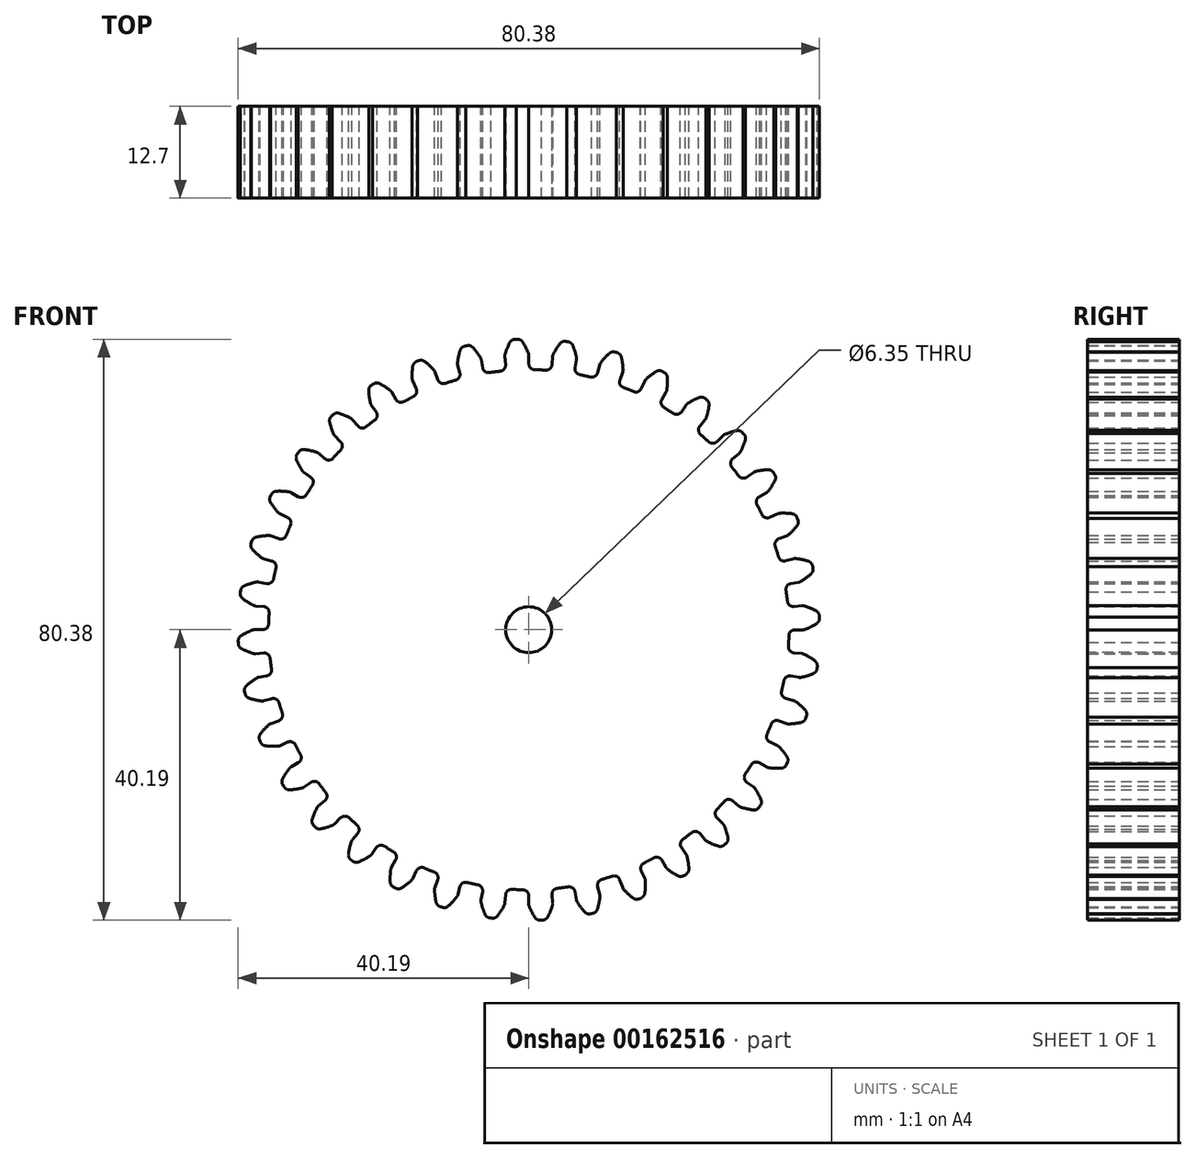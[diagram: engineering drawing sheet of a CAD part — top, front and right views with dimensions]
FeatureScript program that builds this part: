
annotation { "Feature Type Name" : "Feature", "Feature Type Description" : "" }
export const myFeature = defineFeature(function(context is Context, id is Id, definition is map)
    precondition{}
    {
        {
            var Q0;
            Q0=qCreatedBy(makeId("Front.planeOp"),FACE);
            var sketch = newSketch(context, id + "F0", { "sketchPlane" : qUnion([Q0])});
            skArc(sketch, "E0", {"start": v(-3.94, 35.77) * mm, "mid": v(-4.7, 35.68) * mm, "end": v(-5.45, 35.57) * mm});
            skArc(sketch, "E1", {"start": v(-0.05, 38.25) * mm, "mid": v(-0.42, 39.05) * mm, "end": v(-0.85, 39.8) * mm});
            skLineSegment(sketch, "E2", {"start": v(0, 37.94) * mm, "end": v(0, 36.8) * mm});
            skLineSegment(sketch, "E3", {"start": v(-1.58, 40.18) * mm, "end": v(-1.76, 40.18) * mm});
            skLineSegment(sketch, "E4.MirrorCS", {"start": v(-1.93, 40.17) * mm, "end": v(-1.75, 40.18) * mm});
            skArc(sketch, "E5.MirrorCS", {"start": v(-3.28, 38.11) * mm, "mid": v(-2.99, 38.93) * mm, "end": v(-2.62, 39.73) * mm});
            skLineSegment(sketch, "E6.MirrorCS", {"start": v(-3.31, 37.8) * mm, "end": v(-3.21, 36.66) * mm});
            skPoint(sketch, "E7.visualSharp", {"position": v(-3.14, 35.85) * mm});
            skArc(sketch, "E7.filletArc", {"start": v(-3.94, 35.77) * mm, "mid": v(-3.4, 36.07) * mm, "end": v(-3.21, 36.66) * mm});
            skPoint(sketch, "E8.visualSharp", {"position": v(0, 35.98) * mm});
            skArc(sketch, "E8.filletArc", {"start": v(0, 36.8) * mm, "mid": v(0.24, 36.22) * mm, "end": v(0.81, 35.97) * mm});
            skArc(sketch, "E9.filletArc", {"start": v(-1.93, 40.17) * mm, "mid": v(-2.34, 40.04) * mm, "end": v(-2.62, 39.73) * mm});
            skArc(sketch, "E10.filletArc", {"start": v(-0.85, 39.8) * mm, "mid": v(-1.16, 40.1) * mm, "end": v(-1.58, 40.18) * mm});
            skPoint(sketch, "E11.visualSharp", {"position": v(0, 38.1) * mm});
            skArc(sketch, "E11.filletArc", {"start": v(0, 37.94) * mm, "mid": v(0, 38.1) * mm, "end": v(-0.05, 38.25) * mm});
            skPoint(sketch, "E12.visualSharp", {"position": v(-3.33, 37.95) * mm});
            skArc(sketch, "E12.filletArc", {"start": v(-3.28, 38.11) * mm, "mid": v(-3.31, 37.96) * mm, "end": v(-3.31, 37.8) * mm});
            skArc(sketch, "E13.1.0", {"start": v(-10.1, 34.54) * mm, "mid": v(-9.6, 34.93) * mm, "end": v(-9.53, 35.55) * mm});
            skLineSegment(sketch, "E13.1.1", {"start": v(-9.83, 36.65) * mm, "end": v(-9.53, 35.55) * mm});
            skArc(sketch, "E13.1.2", {"start": v(-9.85, 36.96) * mm, "mid": v(-9.85, 36.8) * mm, "end": v(-9.83, 36.65) * mm});
            skArc(sketch, "E13.1.3", {"start": v(-9.85, 36.96) * mm, "mid": v(-9.7, 37.82) * mm, "end": v(-9.48, 38.67) * mm});
            skArc(sketch, "E13.1.4", {"start": v(-8.88, 39.22) * mm, "mid": v(-9.25, 39.03) * mm, "end": v(-9.48, 38.67) * mm});
            skLineSegment(sketch, "E13.1.5", {"start": v(-8.88, 39.22) * mm, "end": v(-8.7, 39.26) * mm});
            skLineSegment(sketch, "E13.1.6", {"start": v(-8.53, 39.3) * mm, "end": v(-8.7, 39.26) * mm});
            skArc(sketch, "E13.1.7", {"start": v(-7.75, 39.05) * mm, "mid": v(-8.1, 39.28) * mm, "end": v(-8.53, 39.3) * mm});
            skArc(sketch, "E13.1.8", {"start": v(-6.7, 37.66) * mm, "mid": v(-7.2, 38.38) * mm, "end": v(-7.75, 39.05) * mm});
            skArc(sketch, "E13.1.9", {"start": v(-6.58, 37.37) * mm, "mid": v(-6.62, 37.52) * mm, "end": v(-6.7, 37.66) * mm});
            skLineSegment(sketch, "E13.1.10", {"start": v(-6.58, 37.37) * mm, "end": v(-6.39, 36.24) * mm});
            skArc(sketch, "E13.1.11", {"start": v(-6.39, 36.24) * mm, "mid": v(-6.06, 35.71) * mm, "end": v(-5.45, 35.57) * mm});
            skArc(sketch, "E13.2.0", {"start": v(-15.94, 32.26) * mm, "mid": v(-15.52, 32.73) * mm, "end": v(-15.56, 33.35) * mm});
            skLineSegment(sketch, "E13.2.1", {"start": v(-16.04, 34.38) * mm, "end": v(-15.56, 33.35) * mm});
            skArc(sketch, "E13.2.2", {"start": v(-16.12, 34.7) * mm, "mid": v(-16.1, 34.53) * mm, "end": v(-16.04, 34.38) * mm});
            skArc(sketch, "E13.2.3", {"start": v(-16.12, 34.7) * mm, "mid": v(-16.13, 35.56) * mm, "end": v(-16.05, 36.43) * mm});
            skArc(sketch, "E13.2.4", {"start": v(-15.55, 37.09) * mm, "mid": v(-15.89, 36.83) * mm, "end": v(-16.05, 36.43) * mm});
            skLineSegment(sketch, "E13.2.5", {"start": v(-15.55, 37.09) * mm, "end": v(-15.39, 37.16) * mm});
            skLineSegment(sketch, "E13.2.6", {"start": v(-15.23, 37.22) * mm, "end": v(-15.4, 37.16) * mm});
            skArc(sketch, "E13.2.7", {"start": v(-14.41, 37.11) * mm, "mid": v(-14.8, 37.28) * mm, "end": v(-15.23, 37.22) * mm});
            skArc(sketch, "E13.2.8", {"start": v(-13.13, 35.93) * mm, "mid": v(-13.75, 36.55) * mm, "end": v(-14.41, 37.11) * mm});
            skArc(sketch, "E13.2.9", {"start": v(-12.97, 35.66) * mm, "mid": v(-13.04, 35.8) * mm, "end": v(-13.13, 35.93) * mm});
            skLineSegment(sketch, "E13.2.10", {"start": v(-12.97, 35.66) * mm, "end": v(-12.58, 34.58) * mm});
            skArc(sketch, "E13.2.11", {"start": v(-12.58, 34.58) * mm, "mid": v(-12.17, 34.12) * mm, "end": v(-11.54, 34.08) * mm});
            skArc(sketch, "E13.3.0", {"start": v(-21.3, 29) * mm, "mid": v(-20.97, 29.54) * mm, "end": v(-21.11, 30.15) * mm});
            skLineSegment(sketch, "E13.3.1", {"start": v(-21.77, 31.08) * mm, "end": v(-21.11, 30.15) * mm});
            skArc(sketch, "E13.3.2", {"start": v(-21.9, 31.37) * mm, "mid": v(-21.85, 31.21) * mm, "end": v(-21.77, 31.08) * mm});
            skArc(sketch, "E13.3.3", {"start": v(-21.9, 31.37) * mm, "mid": v(-22.06, 32.22) * mm, "end": v(-22.13, 33.1) * mm});
            skArc(sketch, "E13.3.4", {"start": v(-21.76, 33.82) * mm, "mid": v(-22.04, 33.5) * mm, "end": v(-22.13, 33.1) * mm});
            skLineSegment(sketch, "E13.3.5", {"start": v(-21.76, 33.82) * mm, "end": v(-21.6, 33.92) * mm});
            skLineSegment(sketch, "E13.3.6", {"start": v(-21.46, 34.01) * mm, "end": v(-21.6, 33.92) * mm});
            skArc(sketch, "E13.3.7", {"start": v(-20.64, 34.05) * mm, "mid": v(-21.05, 34.14) * mm, "end": v(-21.46, 34.01) * mm});
            skArc(sketch, "E13.3.8", {"start": v(-19.17, 33.1) * mm, "mid": v(-19.88, 33.6) * mm, "end": v(-20.64, 34.05) * mm});
            skArc(sketch, "E13.3.9", {"start": v(-18.96, 32.86) * mm, "mid": v(-19.06, 33) * mm, "end": v(-19.17, 33.1) * mm});
            skLineSegment(sketch, "E13.3.10", {"start": v(-18.96, 32.86) * mm, "end": v(-18.4, 31.87) * mm});
            skArc(sketch, "E13.3.11", {"start": v(-18.4, 31.87) * mm, "mid": v(-17.9, 31.49) * mm, "end": v(-17.29, 31.56) * mm});
            skArc(sketch, "E13.4.0", {"start": v(-26.01, 24.86) * mm, "mid": v(-25.78, 25.45) * mm, "end": v(-26.03, 26.02) * mm});
            skLineSegment(sketch, "E13.4.1", {"start": v(-26.83, 26.82) * mm, "end": v(-26.03, 26.02) * mm});
            skArc(sketch, "E13.4.2", {"start": v(-27.01, 27.09) * mm, "mid": v(-26.94, 26.95) * mm, "end": v(-26.83, 26.82) * mm});
            skArc(sketch, "E13.4.3", {"start": v(-27.01, 27.09) * mm, "mid": v(-27.32, 27.9) * mm, "end": v(-27.54, 28.75) * mm});
            skArc(sketch, "E13.4.4", {"start": v(-27.3, 29.53) * mm, "mid": v(-27.53, 29.17) * mm, "end": v(-27.54, 28.75) * mm});
            skLineSegment(sketch, "E13.4.5", {"start": v(-27.3, 29.53) * mm, "end": v(-27.17, 29.65) * mm});
            skLineSegment(sketch, "E13.4.6", {"start": v(-27.04, 29.77) * mm, "end": v(-27.17, 29.65) * mm});
            skArc(sketch, "E13.4.7", {"start": v(-26.24, 29.94) * mm, "mid": v(-26.66, 29.96) * mm, "end": v(-27.04, 29.77) * mm});
            skArc(sketch, "E13.4.8", {"start": v(-24.63, 29.27) * mm, "mid": v(-25.42, 29.64) * mm, "end": v(-26.24, 29.94) * mm});
            skArc(sketch, "E13.4.9", {"start": v(-24.38, 29.07) * mm, "mid": v(-24.5, 29.18) * mm, "end": v(-24.63, 29.27) * mm});
            skLineSegment(sketch, "E13.4.10", {"start": v(-24.38, 29.07) * mm, "end": v(-23.65, 28.2) * mm});
            skArc(sketch, "E13.4.11", {"start": v(-23.65, 28.2) * mm, "mid": v(-23.1, 27.9) * mm, "end": v(-22.5, 28.08) * mm});
            skArc(sketch, "E13.5.0", {"start": v(-29.93, 19.97) * mm, "mid": v(-29.8, 20.58) * mm, "end": v(-30.15, 21.1) * mm});
            skLineSegment(sketch, "E13.5.1", {"start": v(-31.08, 21.76) * mm, "end": v(-30.15, 21.1) * mm});
            skArc(sketch, "E13.5.2", {"start": v(-31.3, 21.98) * mm, "mid": v(-31.2, 21.86) * mm, "end": v(-31.08, 21.76) * mm});
            skArc(sketch, "E13.5.3", {"start": v(-31.3, 21.98) * mm, "mid": v(-31.75, 22.74) * mm, "end": v(-32.12, 23.53) * mm});
            skArc(sketch, "E13.5.4", {"start": v(-32.01, 24.34) * mm, "mid": v(-32.17, 23.95) * mm, "end": v(-32.12, 23.53) * mm});
            skLineSegment(sketch, "E13.5.5", {"start": v(-32.01, 24.34) * mm, "end": v(-31.9, 24.48) * mm});
            skLineSegment(sketch, "E13.5.6", {"start": v(-31.8, 24.62) * mm, "end": v(-31.9, 24.48) * mm});
            skArc(sketch, "E13.5.7", {"start": v(-31.04, 24.93) * mm, "mid": v(-31.46, 24.88) * mm, "end": v(-31.8, 24.62) * mm});
            skArc(sketch, "E13.5.8", {"start": v(-29.34, 24.55) * mm, "mid": v(-30.18, 24.78) * mm, "end": v(-31.04, 24.93) * mm});
            skArc(sketch, "E13.5.9", {"start": v(-29.06, 24.4) * mm, "mid": v(-29.2, 24.49) * mm, "end": v(-29.34, 24.55) * mm});
            skLineSegment(sketch, "E13.5.10", {"start": v(-29.06, 24.4) * mm, "end": v(-28.2, 23.66) * mm});
            skArc(sketch, "E13.5.11", {"start": v(-28.2, 23.66) * mm, "mid": v(-27.6, 23.47) * mm, "end": v(-27.04, 23.74) * mm});
            skArc(sketch, "E13.6.0", {"start": v(-32.95, 14.47) * mm, "mid": v(-32.93, 15.1) * mm, "end": v(-33.36, 15.55) * mm});
            skLineSegment(sketch, "E13.6.1", {"start": v(-34.4, 16.03) * mm, "end": v(-33.36, 15.55) * mm});
            skArc(sketch, "E13.6.2", {"start": v(-34.65, 16.21) * mm, "mid": v(-34.53, 16.1) * mm, "end": v(-34.4, 16.03) * mm});
            skArc(sketch, "E13.6.3", {"start": v(-34.65, 16.21) * mm, "mid": v(-35.21, 16.88) * mm, "end": v(-35.71, 17.6) * mm});
            skArc(sketch, "E13.6.4", {"start": v(-35.75, 18.41) * mm, "mid": v(-35.84, 18) * mm, "end": v(-35.71, 17.6) * mm});
            skLineSegment(sketch, "E13.6.5", {"start": v(-35.75, 18.41) * mm, "end": v(-35.67, 18.57) * mm});
            skLineSegment(sketch, "E13.6.6", {"start": v(-35.59, 18.73) * mm, "end": v(-35.67, 18.57) * mm});
            skArc(sketch, "E13.6.7", {"start": v(-34.9, 19.16) * mm, "mid": v(-35.3, 19.04) * mm, "end": v(-35.59, 18.73) * mm});
            skArc(sketch, "E13.6.8", {"start": v(-33.16, 19.08) * mm, "mid": v(-34.02, 19.16) * mm, "end": v(-34.9, 19.16) * mm});
            skArc(sketch, "E13.6.9", {"start": v(-32.85, 18.98) * mm, "mid": v(-33, 19.04) * mm, "end": v(-33.16, 19.08) * mm});
            skLineSegment(sketch, "E13.6.10", {"start": v(-32.85, 18.98) * mm, "end": v(-31.87, 18.4) * mm});
            skArc(sketch, "E13.6.11", {"start": v(-31.87, 18.4) * mm, "mid": v(-31.25, 18.32) * mm, "end": v(-30.75, 18.69) * mm});
            skArc(sketch, "E13.7.0", {"start": v(-34.96, 8.53) * mm, "mid": v(-35.05, 9.15) * mm, "end": v(-35.55, 9.52) * mm});
            skLineSegment(sketch, "E13.7.1", {"start": v(-36.65, 9.81) * mm, "end": v(-35.55, 9.52) * mm});
            skArc(sketch, "E13.7.2", {"start": v(-36.94, 9.95) * mm, "mid": v(-36.8, 9.87) * mm, "end": v(-36.65, 9.81) * mm});
            skArc(sketch, "E13.7.3", {"start": v(-36.94, 9.95) * mm, "mid": v(-37.6, 10.5) * mm, "end": v(-38.23, 11.12) * mm});
            skArc(sketch, "E13.7.4", {"start": v(-38.4, 11.92) * mm, "mid": v(-38.42, 11.5) * mm, "end": v(-38.23, 11.12) * mm});
            skLineSegment(sketch, "E13.7.5", {"start": v(-38.4, 11.92) * mm, "end": v(-38.36, 12.1) * mm});
            skLineSegment(sketch, "E13.7.6", {"start": v(-38.3, 12.26) * mm, "end": v(-38.36, 12.1) * mm});
            skArc(sketch, "E13.7.7", {"start": v(-37.7, 12.81) * mm, "mid": v(-38.07, 12.62) * mm, "end": v(-38.3, 12.26) * mm});
            skArc(sketch, "E13.7.8", {"start": v(-35.97, 13.03) * mm, "mid": v(-36.83, 12.96) * mm, "end": v(-37.7, 12.81) * mm});
            skArc(sketch, "E13.7.9", {"start": v(-35.65, 12.98) * mm, "mid": v(-35.8, 13.02) * mm, "end": v(-35.97, 13.03) * mm});
            skLineSegment(sketch, "E13.7.10", {"start": v(-35.65, 12.98) * mm, "end": v(-34.58, 12.6) * mm});
            skArc(sketch, "E13.7.11", {"start": v(-34.58, 12.6) * mm, "mid": v(-33.96, 12.61) * mm, "end": v(-33.53, 13.07) * mm});
            skArc(sketch, "E13.8.0", {"start": v(-35.9, 2.33) * mm, "mid": v(-36.1, 2.92) * mm, "end": v(-36.66, 3.2) * mm});
            skLineSegment(sketch, "E13.8.1", {"start": v(-37.8, 3.3) * mm, "end": v(-36.66, 3.2) * mm});
            skArc(sketch, "E13.8.2", {"start": v(-38.1, 3.39) * mm, "mid": v(-37.96, 3.33) * mm, "end": v(-37.8, 3.3) * mm});
            skArc(sketch, "E13.8.3", {"start": v(-38.1, 3.39) * mm, "mid": v(-38.86, 3.82) * mm, "end": v(-39.58, 4.32) * mm});
            skArc(sketch, "E13.8.4", {"start": v(-39.9, 5.07) * mm, "mid": v(-39.84, 4.65) * mm, "end": v(-39.58, 4.32) * mm});
            skLineSegment(sketch, "E13.8.5", {"start": v(-39.9, 5.07) * mm, "end": v(-39.87, 5.25) * mm});
            skLineSegment(sketch, "E13.8.6", {"start": v(-39.85, 5.43) * mm, "end": v(-39.87, 5.25) * mm});
            skArc(sketch, "E13.8.7", {"start": v(-39.35, 6.07) * mm, "mid": v(-39.68, 5.82) * mm, "end": v(-39.85, 5.43) * mm});
            skArc(sketch, "E13.8.8", {"start": v(-37.68, 6.6) * mm, "mid": v(-38.53, 6.37) * mm, "end": v(-39.35, 6.07) * mm});
            skArc(sketch, "E13.8.9", {"start": v(-37.36, 6.6) * mm, "mid": v(-37.52, 6.6) * mm, "end": v(-37.68, 6.6) * mm});
            skLineSegment(sketch, "E13.8.10", {"start": v(-37.36, 6.6) * mm, "end": v(-36.24, 6.4) * mm});
            skArc(sketch, "E13.8.11", {"start": v(-36.24, 6.4) * mm, "mid": v(-35.63, 6.52) * mm, "end": v(-35.29, 7.04) * mm});
            skArc(sketch, "E13.9.0", {"start": v(-35.77, -3.94) * mm, "mid": v(-36.07, -3.4) * mm, "end": v(-36.66, -3.21) * mm});
            skLineSegment(sketch, "E13.9.1", {"start": v(-37.8, -3.31) * mm, "end": v(-36.66, -3.21) * mm});
            skArc(sketch, "E13.9.2", {"start": v(-38.11, -3.28) * mm, "mid": v(-37.96, -3.31) * mm, "end": v(-37.8, -3.31) * mm});
            skArc(sketch, "E13.9.3", {"start": v(-38.11, -3.28) * mm, "mid": v(-38.93, -2.99) * mm, "end": v(-39.73, -2.62) * mm});
            skArc(sketch, "E13.9.4", {"start": v(-40.17, -1.93) * mm, "mid": v(-40.04, -2.34) * mm, "end": v(-39.73, -2.62) * mm});
            skLineSegment(sketch, "E13.9.5", {"start": v(-40.17, -1.93) * mm, "end": v(-40.18, -1.75) * mm});
            skLineSegment(sketch, "E13.9.6", {"start": v(-40.18, -1.58) * mm, "end": v(-40.18, -1.76) * mm});
            skArc(sketch, "E13.9.7", {"start": v(-39.8, -0.85) * mm, "mid": v(-40.1, -1.16) * mm, "end": v(-40.18, -1.58) * mm});
            skArc(sketch, "E13.9.8", {"start": v(-38.25, -0.05) * mm, "mid": v(-39.05, -0.42) * mm, "end": v(-39.8, -0.85) * mm});
            skArc(sketch, "E13.9.9", {"start": v(-37.94, 0) * mm, "mid": v(-38.1, 0) * mm, "end": v(-38.25, -0.05) * mm});
            skLineSegment(sketch, "E13.9.10", {"start": v(-37.94, 0) * mm, "end": v(-36.8, 0) * mm});
            skArc(sketch, "E13.9.11", {"start": v(-36.8, 0) * mm, "mid": v(-36.22, 0.24) * mm, "end": v(-35.97, 0.81) * mm});
            skArc(sketch, "E13.10.0", {"start": v(-34.54, -10.1) * mm, "mid": v(-34.93, -9.6) * mm, "end": v(-35.55, -9.53) * mm});
            skLineSegment(sketch, "E13.10.1", {"start": v(-36.65, -9.83) * mm, "end": v(-35.55, -9.53) * mm});
            skArc(sketch, "E13.10.2", {"start": v(-36.96, -9.85) * mm, "mid": v(-36.8, -9.85) * mm, "end": v(-36.65, -9.83) * mm});
            skArc(sketch, "E13.10.3", {"start": v(-36.96, -9.85) * mm, "mid": v(-37.82, -9.7) * mm, "end": v(-38.67, -9.48) * mm});
            skArc(sketch, "E13.10.4", {"start": v(-39.22, -8.88) * mm, "mid": v(-39.03, -9.25) * mm, "end": v(-38.67, -9.48) * mm});
            skLineSegment(sketch, "E13.10.5", {"start": v(-39.22, -8.88) * mm, "end": v(-39.26, -8.7) * mm});
            skLineSegment(sketch, "E13.10.6", {"start": v(-39.3, -8.53) * mm, "end": v(-39.26, -8.7) * mm});
            skArc(sketch, "E13.10.7", {"start": v(-39.05, -7.75) * mm, "mid": v(-39.28, -8.1) * mm, "end": v(-39.3, -8.53) * mm});
            skArc(sketch, "E13.10.8", {"start": v(-37.66, -6.7) * mm, "mid": v(-38.38, -7.2) * mm, "end": v(-39.05, -7.75) * mm});
            skArc(sketch, "E13.10.9", {"start": v(-37.37, -6.58) * mm, "mid": v(-37.52, -6.62) * mm, "end": v(-37.66, -6.7) * mm});
            skLineSegment(sketch, "E13.10.10", {"start": v(-37.37, -6.58) * mm, "end": v(-36.24, -6.39) * mm});
            skArc(sketch, "E13.10.11", {"start": v(-36.24, -6.39) * mm, "mid": v(-35.71, -6.06) * mm, "end": v(-35.57, -5.45) * mm});
            skArc(sketch, "E13.11.0", {"start": v(-32.26, -15.94) * mm, "mid": v(-32.73, -15.52) * mm, "end": v(-33.35, -15.56) * mm});
            skLineSegment(sketch, "E13.11.1", {"start": v(-34.38, -16.04) * mm, "end": v(-33.35, -15.56) * mm});
            skArc(sketch, "E13.11.2", {"start": v(-34.7, -16.12) * mm, "mid": v(-34.53, -16.1) * mm, "end": v(-34.38, -16.04) * mm});
            skArc(sketch, "E13.11.3", {"start": v(-34.7, -16.12) * mm, "mid": v(-35.56, -16.13) * mm, "end": v(-36.43, -16.05) * mm});
            skArc(sketch, "E13.11.4", {"start": v(-37.09, -15.55) * mm, "mid": v(-36.83, -15.89) * mm, "end": v(-36.43, -16.05) * mm});
            skLineSegment(sketch, "E13.11.5", {"start": v(-37.09, -15.55) * mm, "end": v(-37.16, -15.39) * mm});
            skLineSegment(sketch, "E13.11.6", {"start": v(-37.22, -15.23) * mm, "end": v(-37.16, -15.4) * mm});
            skArc(sketch, "E13.11.7", {"start": v(-37.11, -14.41) * mm, "mid": v(-37.28, -14.8) * mm, "end": v(-37.22, -15.23) * mm});
            skArc(sketch, "E13.11.8", {"start": v(-35.93, -13.13) * mm, "mid": v(-36.55, -13.75) * mm, "end": v(-37.11, -14.41) * mm});
            skArc(sketch, "E13.11.9", {"start": v(-35.66, -12.97) * mm, "mid": v(-35.8, -13.04) * mm, "end": v(-35.93, -13.13) * mm});
            skLineSegment(sketch, "E13.11.10", {"start": v(-35.66, -12.97) * mm, "end": v(-34.58, -12.58) * mm});
            skArc(sketch, "E13.11.11", {"start": v(-34.58, -12.58) * mm, "mid": v(-34.12, -12.17) * mm, "end": v(-34.08, -11.54) * mm});
            skArc(sketch, "E13.12.0", {"start": v(-29, -21.3) * mm, "mid": v(-29.54, -20.97) * mm, "end": v(-30.15, -21.11) * mm});
            skLineSegment(sketch, "E13.12.1", {"start": v(-31.08, -21.77) * mm, "end": v(-30.15, -21.11) * mm});
            skArc(sketch, "E13.12.2", {"start": v(-31.37, -21.9) * mm, "mid": v(-31.21, -21.85) * mm, "end": v(-31.08, -21.77) * mm});
            skArc(sketch, "E13.12.3", {"start": v(-31.37, -21.9) * mm, "mid": v(-32.22, -22.06) * mm, "end": v(-33.1, -22.13) * mm});
            skArc(sketch, "E13.12.4", {"start": v(-33.82, -21.76) * mm, "mid": v(-33.5, -22.04) * mm, "end": v(-33.1, -22.13) * mm});
            skLineSegment(sketch, "E13.12.5", {"start": v(-33.82, -21.76) * mm, "end": v(-33.92, -21.6) * mm});
            skLineSegment(sketch, "E13.12.6", {"start": v(-34.01, -21.46) * mm, "end": v(-33.92, -21.6) * mm});
            skArc(sketch, "E13.12.7", {"start": v(-34.05, -20.64) * mm, "mid": v(-34.14, -21.05) * mm, "end": v(-34.01, -21.46) * mm});
            skArc(sketch, "E13.12.8", {"start": v(-33.1, -19.17) * mm, "mid": v(-33.6, -19.88) * mm, "end": v(-34.05, -20.64) * mm});
            skArc(sketch, "E13.12.9", {"start": v(-32.86, -18.96) * mm, "mid": v(-33, -19.06) * mm, "end": v(-33.1, -19.17) * mm});
            skLineSegment(sketch, "E13.12.10", {"start": v(-32.86, -18.96) * mm, "end": v(-31.87, -18.4) * mm});
            skArc(sketch, "E13.12.11", {"start": v(-31.87, -18.4) * mm, "mid": v(-31.49, -17.9) * mm, "end": v(-31.56, -17.29) * mm});
            skArc(sketch, "E13.13.0", {"start": v(-24.86, -26.01) * mm, "mid": v(-25.45, -25.78) * mm, "end": v(-26.02, -26.03) * mm});
            skLineSegment(sketch, "E13.13.1", {"start": v(-26.82, -26.83) * mm, "end": v(-26.02, -26.03) * mm});
            skArc(sketch, "E13.13.2", {"start": v(-27.09, -27.01) * mm, "mid": v(-26.95, -26.94) * mm, "end": v(-26.82, -26.83) * mm});
            skArc(sketch, "E13.13.3", {"start": v(-27.09, -27.01) * mm, "mid": v(-27.9, -27.32) * mm, "end": v(-28.75, -27.54) * mm});
            skArc(sketch, "E13.13.4", {"start": v(-29.53, -27.3) * mm, "mid": v(-29.17, -27.53) * mm, "end": v(-28.75, -27.54) * mm});
            skLineSegment(sketch, "E13.13.5", {"start": v(-29.53, -27.3) * mm, "end": v(-29.65, -27.17) * mm});
            skLineSegment(sketch, "E13.13.6", {"start": v(-29.77, -27.04) * mm, "end": v(-29.65, -27.17) * mm});
            skArc(sketch, "E13.13.7", {"start": v(-29.94, -26.24) * mm, "mid": v(-29.96, -26.66) * mm, "end": v(-29.77, -27.04) * mm});
            skArc(sketch, "E13.13.8", {"start": v(-29.27, -24.63) * mm, "mid": v(-29.64, -25.42) * mm, "end": v(-29.94, -26.24) * mm});
            skArc(sketch, "E13.13.9", {"start": v(-29.07, -24.38) * mm, "mid": v(-29.18, -24.5) * mm, "end": v(-29.27, -24.63) * mm});
            skLineSegment(sketch, "E13.13.10", {"start": v(-29.07, -24.38) * mm, "end": v(-28.2, -23.65) * mm});
            skArc(sketch, "E13.13.11", {"start": v(-28.2, -23.65) * mm, "mid": v(-27.9, -23.1) * mm, "end": v(-28.08, -22.5) * mm});
            skArc(sketch, "E13.14.0", {"start": v(-19.97, -29.93) * mm, "mid": v(-20.58, -29.8) * mm, "end": v(-21.1, -30.15) * mm});
            skLineSegment(sketch, "E13.14.1", {"start": v(-21.76, -31.08) * mm, "end": v(-21.1, -30.15) * mm});
            skArc(sketch, "E13.14.2", {"start": v(-21.98, -31.3) * mm, "mid": v(-21.86, -31.2) * mm, "end": v(-21.76, -31.08) * mm});
            skArc(sketch, "E13.14.3", {"start": v(-21.98, -31.3) * mm, "mid": v(-22.74, -31.75) * mm, "end": v(-23.53, -32.12) * mm});
            skArc(sketch, "E13.14.4", {"start": v(-24.34, -32.01) * mm, "mid": v(-23.95, -32.17) * mm, "end": v(-23.53, -32.12) * mm});
            skLineSegment(sketch, "E13.14.5", {"start": v(-24.34, -32.01) * mm, "end": v(-24.48, -31.9) * mm});
            skLineSegment(sketch, "E13.14.6", {"start": v(-24.62, -31.8) * mm, "end": v(-24.48, -31.9) * mm});
            skArc(sketch, "E13.14.7", {"start": v(-24.93, -31.04) * mm, "mid": v(-24.88, -31.46) * mm, "end": v(-24.62, -31.8) * mm});
            skArc(sketch, "E13.14.8", {"start": v(-24.55, -29.34) * mm, "mid": v(-24.78, -30.18) * mm, "end": v(-24.93, -31.04) * mm});
            skArc(sketch, "E13.14.9", {"start": v(-24.4, -29.06) * mm, "mid": v(-24.49, -29.2) * mm, "end": v(-24.55, -29.34) * mm});
            skLineSegment(sketch, "E13.14.10", {"start": v(-24.4, -29.06) * mm, "end": v(-23.66, -28.2) * mm});
            skArc(sketch, "E13.14.11", {"start": v(-23.66, -28.2) * mm, "mid": v(-23.47, -27.6) * mm, "end": v(-23.74, -27.04) * mm});
            skArc(sketch, "E13.15.0", {"start": v(-14.47, -32.95) * mm, "mid": v(-15.1, -32.93) * mm, "end": v(-15.55, -33.36) * mm});
            skLineSegment(sketch, "E13.15.1", {"start": v(-16.03, -34.4) * mm, "end": v(-15.55, -33.36) * mm});
            skArc(sketch, "E13.15.2", {"start": v(-16.21, -34.65) * mm, "mid": v(-16.1, -34.53) * mm, "end": v(-16.03, -34.4) * mm});
            skArc(sketch, "E13.15.3", {"start": v(-16.21, -34.65) * mm, "mid": v(-16.88, -35.21) * mm, "end": v(-17.6, -35.71) * mm});
            skArc(sketch, "E13.15.4", {"start": v(-18.41, -35.75) * mm, "mid": v(-18, -35.84) * mm, "end": v(-17.6, -35.71) * mm});
            skLineSegment(sketch, "E13.15.5", {"start": v(-18.41, -35.75) * mm, "end": v(-18.57, -35.67) * mm});
            skLineSegment(sketch, "E13.15.6", {"start": v(-18.73, -35.59) * mm, "end": v(-18.57, -35.67) * mm});
            skArc(sketch, "E13.15.7", {"start": v(-19.16, -34.9) * mm, "mid": v(-19.04, -35.3) * mm, "end": v(-18.73, -35.59) * mm});
            skArc(sketch, "E13.15.8", {"start": v(-19.08, -33.16) * mm, "mid": v(-19.16, -34.02) * mm, "end": v(-19.16, -34.9) * mm});
            skArc(sketch, "E13.15.9", {"start": v(-18.98, -32.85) * mm, "mid": v(-19.04, -33) * mm, "end": v(-19.08, -33.16) * mm});
            skLineSegment(sketch, "E13.15.10", {"start": v(-18.98, -32.85) * mm, "end": v(-18.4, -31.87) * mm});
            skArc(sketch, "E13.15.11", {"start": v(-18.4, -31.87) * mm, "mid": v(-18.32, -31.25) * mm, "end": v(-18.69, -30.75) * mm});
            skArc(sketch, "E13.16.0", {"start": v(-8.53, -34.96) * mm, "mid": v(-9.15, -35.05) * mm, "end": v(-9.52, -35.55) * mm});
            skLineSegment(sketch, "E13.16.1", {"start": v(-9.81, -36.65) * mm, "end": v(-9.52, -35.55) * mm});
            skArc(sketch, "E13.16.2", {"start": v(-9.95, -36.94) * mm, "mid": v(-9.87, -36.8) * mm, "end": v(-9.81, -36.65) * mm});
            skArc(sketch, "E13.16.3", {"start": v(-9.95, -36.94) * mm, "mid": v(-10.5, -37.6) * mm, "end": v(-11.12, -38.23) * mm});
            skArc(sketch, "E13.16.4", {"start": v(-11.92, -38.4) * mm, "mid": v(-11.5, -38.42) * mm, "end": v(-11.12, -38.23) * mm});
            skLineSegment(sketch, "E13.16.5", {"start": v(-11.92, -38.4) * mm, "end": v(-12.1, -38.36) * mm});
            skLineSegment(sketch, "E13.16.6", {"start": v(-12.26, -38.3) * mm, "end": v(-12.1, -38.36) * mm});
            skArc(sketch, "E13.16.7", {"start": v(-12.81, -37.7) * mm, "mid": v(-12.62, -38.07) * mm, "end": v(-12.26, -38.3) * mm});
            skArc(sketch, "E13.16.8", {"start": v(-13.03, -35.97) * mm, "mid": v(-12.96, -36.83) * mm, "end": v(-12.81, -37.7) * mm});
            skArc(sketch, "E13.16.9", {"start": v(-12.98, -35.65) * mm, "mid": v(-13.02, -35.8) * mm, "end": v(-13.03, -35.97) * mm});
            skLineSegment(sketch, "E13.16.10", {"start": v(-12.98, -35.65) * mm, "end": v(-12.6, -34.58) * mm});
            skArc(sketch, "E13.16.11", {"start": v(-12.6, -34.58) * mm, "mid": v(-12.61, -33.96) * mm, "end": v(-13.07, -33.53) * mm});
            skArc(sketch, "E13.17.0", {"start": v(-2.33, -35.9) * mm, "mid": v(-2.92, -36.1) * mm, "end": v(-3.2, -36.66) * mm});
            skLineSegment(sketch, "E13.17.1", {"start": v(-3.3, -37.8) * mm, "end": v(-3.2, -36.66) * mm});
            skArc(sketch, "E13.17.2", {"start": v(-3.39, -38.1) * mm, "mid": v(-3.33, -37.96) * mm, "end": v(-3.3, -37.8) * mm});
            skArc(sketch, "E13.17.3", {"start": v(-3.39, -38.1) * mm, "mid": v(-3.82, -38.86) * mm, "end": v(-4.32, -39.58) * mm});
            skArc(sketch, "E13.17.4", {"start": v(-5.07, -39.9) * mm, "mid": v(-4.65, -39.84) * mm, "end": v(-4.32, -39.58) * mm});
            skLineSegment(sketch, "E13.17.5", {"start": v(-5.07, -39.9) * mm, "end": v(-5.25, -39.87) * mm});
            skLineSegment(sketch, "E13.17.6", {"start": v(-5.43, -39.85) * mm, "end": v(-5.25, -39.87) * mm});
            skArc(sketch, "E13.17.7", {"start": v(-6.07, -39.35) * mm, "mid": v(-5.82, -39.68) * mm, "end": v(-5.43, -39.85) * mm});
            skArc(sketch, "E13.17.8", {"start": v(-6.6, -37.68) * mm, "mid": v(-6.37, -38.53) * mm, "end": v(-6.07, -39.35) * mm});
            skArc(sketch, "E13.17.9", {"start": v(-6.6, -37.36) * mm, "mid": v(-6.6, -37.52) * mm, "end": v(-6.6, -37.68) * mm});
            skLineSegment(sketch, "E13.17.10", {"start": v(-6.6, -37.36) * mm, "end": v(-6.4, -36.24) * mm});
            skArc(sketch, "E13.17.11", {"start": v(-6.4, -36.24) * mm, "mid": v(-6.52, -35.63) * mm, "end": v(-7.04, -35.29) * mm});
            skArc(sketch, "E13.18.0", {"start": v(3.94, -35.77) * mm, "mid": v(3.4, -36.07) * mm, "end": v(3.21, -36.66) * mm});
            skLineSegment(sketch, "E13.18.1", {"start": v(3.31, -37.8) * mm, "end": v(3.21, -36.66) * mm});
            skArc(sketch, "E13.18.2", {"start": v(3.28, -38.11) * mm, "mid": v(3.31, -37.96) * mm, "end": v(3.31, -37.8) * mm});
            skArc(sketch, "E13.18.3", {"start": v(3.28, -38.11) * mm, "mid": v(2.99, -38.93) * mm, "end": v(2.62, -39.73) * mm});
            skArc(sketch, "E13.18.4", {"start": v(1.93, -40.17) * mm, "mid": v(2.34, -40.04) * mm, "end": v(2.62, -39.73) * mm});
            skLineSegment(sketch, "E13.18.5", {"start": v(1.93, -40.17) * mm, "end": v(1.75, -40.18) * mm});
            skLineSegment(sketch, "E13.18.6", {"start": v(1.58, -40.18) * mm, "end": v(1.76, -40.18) * mm});
            skArc(sketch, "E13.18.7", {"start": v(0.85, -39.8) * mm, "mid": v(1.16, -40.1) * mm, "end": v(1.58, -40.18) * mm});
            skArc(sketch, "E13.18.8", {"start": v(0.05, -38.25) * mm, "mid": v(0.42, -39.05) * mm, "end": v(0.85, -39.8) * mm});
            skArc(sketch, "E13.18.9", {"start": v(0, -37.94) * mm, "mid": v(0, -38.1) * mm, "end": v(0.05, -38.25) * mm});
            skLineSegment(sketch, "E13.18.10", {"start": v(0, -37.94) * mm, "end": v(0, -36.8) * mm});
            skArc(sketch, "E13.18.11", {"start": v(0, -36.8) * mm, "mid": v(-0.24, -36.22) * mm, "end": v(-0.81, -35.97) * mm});
            skArc(sketch, "E13.19.0", {"start": v(10.1, -34.54) * mm, "mid": v(9.6, -34.93) * mm, "end": v(9.53, -35.55) * mm});
            skLineSegment(sketch, "E13.19.1", {"start": v(9.83, -36.65) * mm, "end": v(9.53, -35.55) * mm});
            skArc(sketch, "E13.19.2", {"start": v(9.85, -36.96) * mm, "mid": v(9.85, -36.8) * mm, "end": v(9.83, -36.65) * mm});
            skArc(sketch, "E13.19.3", {"start": v(9.85, -36.96) * mm, "mid": v(9.7, -37.82) * mm, "end": v(9.48, -38.67) * mm});
            skArc(sketch, "E13.19.4", {"start": v(8.88, -39.22) * mm, "mid": v(9.25, -39.03) * mm, "end": v(9.48, -38.67) * mm});
            skLineSegment(sketch, "E13.19.5", {"start": v(8.88, -39.22) * mm, "end": v(8.7, -39.26) * mm});
            skLineSegment(sketch, "E13.19.6", {"start": v(8.53, -39.3) * mm, "end": v(8.7, -39.26) * mm});
            skArc(sketch, "E13.19.7", {"start": v(7.75, -39.05) * mm, "mid": v(8.1, -39.28) * mm, "end": v(8.53, -39.3) * mm});
            skArc(sketch, "E13.19.8", {"start": v(6.7, -37.66) * mm, "mid": v(7.2, -38.38) * mm, "end": v(7.75, -39.05) * mm});
            skArc(sketch, "E13.19.9", {"start": v(6.58, -37.37) * mm, "mid": v(6.62, -37.52) * mm, "end": v(6.7, -37.66) * mm});
            skLineSegment(sketch, "E13.19.10", {"start": v(6.58, -37.37) * mm, "end": v(6.39, -36.24) * mm});
            skArc(sketch, "E13.19.11", {"start": v(6.39, -36.24) * mm, "mid": v(6.06, -35.71) * mm, "end": v(5.45, -35.57) * mm});
            skArc(sketch, "E13.20.0", {"start": v(15.94, -32.26) * mm, "mid": v(15.52, -32.73) * mm, "end": v(15.56, -33.35) * mm});
            skLineSegment(sketch, "E13.20.1", {"start": v(16.04, -34.38) * mm, "end": v(15.56, -33.35) * mm});
            skArc(sketch, "E13.20.2", {"start": v(16.12, -34.7) * mm, "mid": v(16.1, -34.53) * mm, "end": v(16.04, -34.38) * mm});
            skArc(sketch, "E13.20.3", {"start": v(16.12, -34.7) * mm, "mid": v(16.13, -35.56) * mm, "end": v(16.05, -36.43) * mm});
            skArc(sketch, "E13.20.4", {"start": v(15.55, -37.09) * mm, "mid": v(15.89, -36.83) * mm, "end": v(16.05, -36.43) * mm});
            skLineSegment(sketch, "E13.20.5", {"start": v(15.55, -37.09) * mm, "end": v(15.39, -37.16) * mm});
            skLineSegment(sketch, "E13.20.6", {"start": v(15.23, -37.22) * mm, "end": v(15.4, -37.16) * mm});
            skArc(sketch, "E13.20.7", {"start": v(14.41, -37.11) * mm, "mid": v(14.8, -37.28) * mm, "end": v(15.23, -37.22) * mm});
            skArc(sketch, "E13.20.8", {"start": v(13.13, -35.93) * mm, "mid": v(13.75, -36.55) * mm, "end": v(14.41, -37.11) * mm});
            skArc(sketch, "E13.20.9", {"start": v(12.97, -35.66) * mm, "mid": v(13.04, -35.8) * mm, "end": v(13.13, -35.93) * mm});
            skLineSegment(sketch, "E13.20.10", {"start": v(12.97, -35.66) * mm, "end": v(12.58, -34.58) * mm});
            skArc(sketch, "E13.20.11", {"start": v(12.58, -34.58) * mm, "mid": v(12.17, -34.12) * mm, "end": v(11.54, -34.08) * mm});
            skArc(sketch, "E13.21.0", {"start": v(21.3, -29) * mm, "mid": v(20.97, -29.54) * mm, "end": v(21.11, -30.15) * mm});
            skLineSegment(sketch, "E13.21.1", {"start": v(21.77, -31.08) * mm, "end": v(21.11, -30.15) * mm});
            skArc(sketch, "E13.21.2", {"start": v(21.9, -31.37) * mm, "mid": v(21.85, -31.21) * mm, "end": v(21.77, -31.08) * mm});
            skArc(sketch, "E13.21.3", {"start": v(21.9, -31.37) * mm, "mid": v(22.06, -32.22) * mm, "end": v(22.13, -33.1) * mm});
            skArc(sketch, "E13.21.4", {"start": v(21.76, -33.82) * mm, "mid": v(22.04, -33.5) * mm, "end": v(22.13, -33.1) * mm});
            skLineSegment(sketch, "E13.21.5", {"start": v(21.76, -33.82) * mm, "end": v(21.6, -33.92) * mm});
            skLineSegment(sketch, "E13.21.6", {"start": v(21.46, -34.01) * mm, "end": v(21.6, -33.92) * mm});
            skArc(sketch, "E13.21.7", {"start": v(20.64, -34.05) * mm, "mid": v(21.05, -34.14) * mm, "end": v(21.46, -34.01) * mm});
            skArc(sketch, "E13.21.8", {"start": v(19.17, -33.1) * mm, "mid": v(19.88, -33.6) * mm, "end": v(20.64, -34.05) * mm});
            skArc(sketch, "E13.21.9", {"start": v(18.96, -32.86) * mm, "mid": v(19.06, -33) * mm, "end": v(19.17, -33.1) * mm});
            skLineSegment(sketch, "E13.21.10", {"start": v(18.96, -32.86) * mm, "end": v(18.4, -31.87) * mm});
            skArc(sketch, "E13.21.11", {"start": v(18.4, -31.87) * mm, "mid": v(17.9, -31.49) * mm, "end": v(17.29, -31.56) * mm});
            skArc(sketch, "E13.22.0", {"start": v(26.01, -24.86) * mm, "mid": v(25.78, -25.45) * mm, "end": v(26.03, -26.02) * mm});
            skLineSegment(sketch, "E13.22.1", {"start": v(26.83, -26.82) * mm, "end": v(26.03, -26.02) * mm});
            skArc(sketch, "E13.22.2", {"start": v(27.01, -27.09) * mm, "mid": v(26.94, -26.95) * mm, "end": v(26.83, -26.82) * mm});
            skArc(sketch, "E13.22.3", {"start": v(27.01, -27.09) * mm, "mid": v(27.32, -27.9) * mm, "end": v(27.54, -28.75) * mm});
            skArc(sketch, "E13.22.4", {"start": v(27.3, -29.53) * mm, "mid": v(27.53, -29.17) * mm, "end": v(27.54, -28.75) * mm});
            skLineSegment(sketch, "E13.22.5", {"start": v(27.3, -29.53) * mm, "end": v(27.17, -29.65) * mm});
            skLineSegment(sketch, "E13.22.6", {"start": v(27.04, -29.77) * mm, "end": v(27.17, -29.65) * mm});
            skArc(sketch, "E13.22.7", {"start": v(26.24, -29.94) * mm, "mid": v(26.66, -29.96) * mm, "end": v(27.04, -29.77) * mm});
            skArc(sketch, "E13.22.8", {"start": v(24.63, -29.27) * mm, "mid": v(25.42, -29.64) * mm, "end": v(26.24, -29.94) * mm});
            skArc(sketch, "E13.22.9", {"start": v(24.38, -29.07) * mm, "mid": v(24.5, -29.18) * mm, "end": v(24.63, -29.27) * mm});
            skLineSegment(sketch, "E13.22.10", {"start": v(24.38, -29.07) * mm, "end": v(23.65, -28.2) * mm});
            skArc(sketch, "E13.22.11", {"start": v(23.65, -28.2) * mm, "mid": v(23.1, -27.9) * mm, "end": v(22.5, -28.08) * mm});
            skArc(sketch, "E13.23.0", {"start": v(29.93, -19.97) * mm, "mid": v(29.8, -20.58) * mm, "end": v(30.15, -21.1) * mm});
            skLineSegment(sketch, "E13.23.1", {"start": v(31.08, -21.76) * mm, "end": v(30.15, -21.1) * mm});
            skArc(sketch, "E13.23.2", {"start": v(31.3, -21.98) * mm, "mid": v(31.2, -21.86) * mm, "end": v(31.08, -21.76) * mm});
            skArc(sketch, "E13.23.3", {"start": v(31.3, -21.98) * mm, "mid": v(31.75, -22.74) * mm, "end": v(32.12, -23.53) * mm});
            skArc(sketch, "E13.23.4", {"start": v(32.01, -24.34) * mm, "mid": v(32.17, -23.95) * mm, "end": v(32.12, -23.53) * mm});
            skLineSegment(sketch, "E13.23.5", {"start": v(32.01, -24.34) * mm, "end": v(31.9, -24.48) * mm});
            skLineSegment(sketch, "E13.23.6", {"start": v(31.8, -24.62) * mm, "end": v(31.9, -24.48) * mm});
            skArc(sketch, "E13.23.7", {"start": v(31.04, -24.93) * mm, "mid": v(31.46, -24.88) * mm, "end": v(31.8, -24.62) * mm});
            skArc(sketch, "E13.23.8", {"start": v(29.34, -24.55) * mm, "mid": v(30.18, -24.78) * mm, "end": v(31.04, -24.93) * mm});
            skArc(sketch, "E13.23.9", {"start": v(29.06, -24.4) * mm, "mid": v(29.2, -24.49) * mm, "end": v(29.34, -24.55) * mm});
            skLineSegment(sketch, "E13.23.10", {"start": v(29.06, -24.4) * mm, "end": v(28.2, -23.66) * mm});
            skArc(sketch, "E13.23.11", {"start": v(28.2, -23.66) * mm, "mid": v(27.6, -23.47) * mm, "end": v(27.04, -23.74) * mm});
            skArc(sketch, "E13.24.0", {"start": v(32.95, -14.47) * mm, "mid": v(32.93, -15.1) * mm, "end": v(33.36, -15.55) * mm});
            skLineSegment(sketch, "E13.24.1", {"start": v(34.4, -16.03) * mm, "end": v(33.36, -15.55) * mm});
            skArc(sketch, "E13.24.2", {"start": v(34.65, -16.21) * mm, "mid": v(34.53, -16.1) * mm, "end": v(34.4, -16.03) * mm});
            skArc(sketch, "E13.24.3", {"start": v(34.65, -16.21) * mm, "mid": v(35.21, -16.88) * mm, "end": v(35.71, -17.6) * mm});
            skArc(sketch, "E13.24.4", {"start": v(35.75, -18.41) * mm, "mid": v(35.84, -18) * mm, "end": v(35.71, -17.6) * mm});
            skLineSegment(sketch, "E13.24.5", {"start": v(35.75, -18.41) * mm, "end": v(35.67, -18.57) * mm});
            skLineSegment(sketch, "E13.24.6", {"start": v(35.59, -18.73) * mm, "end": v(35.67, -18.57) * mm});
            skArc(sketch, "E13.24.7", {"start": v(34.9, -19.16) * mm, "mid": v(35.3, -19.04) * mm, "end": v(35.59, -18.73) * mm});
            skArc(sketch, "E13.24.8", {"start": v(33.16, -19.08) * mm, "mid": v(34.02, -19.16) * mm, "end": v(34.9, -19.16) * mm});
            skArc(sketch, "E13.24.9", {"start": v(32.85, -18.98) * mm, "mid": v(33, -19.04) * mm, "end": v(33.16, -19.08) * mm});
            skLineSegment(sketch, "E13.24.10", {"start": v(32.85, -18.98) * mm, "end": v(31.87, -18.4) * mm});
            skArc(sketch, "E13.24.11", {"start": v(31.87, -18.4) * mm, "mid": v(31.25, -18.32) * mm, "end": v(30.75, -18.69) * mm});
            skArc(sketch, "E13.25.0", {"start": v(34.96, -8.53) * mm, "mid": v(35.05, -9.15) * mm, "end": v(35.55, -9.52) * mm});
            skLineSegment(sketch, "E13.25.1", {"start": v(36.65, -9.81) * mm, "end": v(35.55, -9.52) * mm});
            skArc(sketch, "E13.25.2", {"start": v(36.94, -9.95) * mm, "mid": v(36.8, -9.87) * mm, "end": v(36.65, -9.81) * mm});
            skArc(sketch, "E13.25.3", {"start": v(36.94, -9.95) * mm, "mid": v(37.6, -10.5) * mm, "end": v(38.23, -11.12) * mm});
            skArc(sketch, "E13.25.4", {"start": v(38.4, -11.92) * mm, "mid": v(38.42, -11.5) * mm, "end": v(38.23, -11.12) * mm});
            skLineSegment(sketch, "E13.25.5", {"start": v(38.4, -11.92) * mm, "end": v(38.36, -12.1) * mm});
            skLineSegment(sketch, "E13.25.6", {"start": v(38.3, -12.26) * mm, "end": v(38.36, -12.1) * mm});
            skArc(sketch, "E13.25.7", {"start": v(37.7, -12.81) * mm, "mid": v(38.07, -12.62) * mm, "end": v(38.3, -12.26) * mm});
            skArc(sketch, "E13.25.8", {"start": v(35.97, -13.03) * mm, "mid": v(36.83, -12.96) * mm, "end": v(37.7, -12.81) * mm});
            skArc(sketch, "E13.25.9", {"start": v(35.65, -12.98) * mm, "mid": v(35.8, -13.02) * mm, "end": v(35.97, -13.03) * mm});
            skLineSegment(sketch, "E13.25.10", {"start": v(35.65, -12.98) * mm, "end": v(34.58, -12.6) * mm});
            skArc(sketch, "E13.25.11", {"start": v(34.58, -12.6) * mm, "mid": v(33.96, -12.61) * mm, "end": v(33.53, -13.07) * mm});
            skArc(sketch, "E13.26.0", {"start": v(35.9, -2.33) * mm, "mid": v(36.1, -2.92) * mm, "end": v(36.66, -3.2) * mm});
            skLineSegment(sketch, "E13.26.1", {"start": v(37.8, -3.3) * mm, "end": v(36.66, -3.2) * mm});
            skArc(sketch, "E13.26.2", {"start": v(38.1, -3.39) * mm, "mid": v(37.96, -3.33) * mm, "end": v(37.8, -3.3) * mm});
            skArc(sketch, "E13.26.3", {"start": v(38.1, -3.39) * mm, "mid": v(38.86, -3.82) * mm, "end": v(39.58, -4.32) * mm});
            skArc(sketch, "E13.26.4", {"start": v(39.9, -5.07) * mm, "mid": v(39.84, -4.65) * mm, "end": v(39.58, -4.32) * mm});
            skLineSegment(sketch, "E13.26.5", {"start": v(39.9, -5.07) * mm, "end": v(39.87, -5.25) * mm});
            skLineSegment(sketch, "E13.26.6", {"start": v(39.85, -5.43) * mm, "end": v(39.87, -5.25) * mm});
            skArc(sketch, "E13.26.7", {"start": v(39.35, -6.07) * mm, "mid": v(39.68, -5.82) * mm, "end": v(39.85, -5.43) * mm});
            skArc(sketch, "E13.26.8", {"start": v(37.68, -6.6) * mm, "mid": v(38.53, -6.37) * mm, "end": v(39.35, -6.07) * mm});
            skArc(sketch, "E13.26.9", {"start": v(37.36, -6.6) * mm, "mid": v(37.52, -6.6) * mm, "end": v(37.68, -6.6) * mm});
            skLineSegment(sketch, "E13.26.10", {"start": v(37.36, -6.6) * mm, "end": v(36.24, -6.4) * mm});
            skArc(sketch, "E13.26.11", {"start": v(36.24, -6.4) * mm, "mid": v(35.63, -6.52) * mm, "end": v(35.29, -7.04) * mm});
            skArc(sketch, "E13.27.0", {"start": v(35.77, 3.94) * mm, "mid": v(36.07, 3.4) * mm, "end": v(36.66, 3.21) * mm});
            skLineSegment(sketch, "E13.27.1", {"start": v(37.8, 3.31) * mm, "end": v(36.66, 3.21) * mm});
            skArc(sketch, "E13.27.2", {"start": v(38.11, 3.28) * mm, "mid": v(37.96, 3.31) * mm, "end": v(37.8, 3.31) * mm});
            skArc(sketch, "E13.27.3", {"start": v(38.11, 3.28) * mm, "mid": v(38.93, 2.99) * mm, "end": v(39.73, 2.62) * mm});
            skArc(sketch, "E13.27.4", {"start": v(40.17, 1.93) * mm, "mid": v(40.04, 2.34) * mm, "end": v(39.73, 2.62) * mm});
            skLineSegment(sketch, "E13.27.5", {"start": v(40.17, 1.93) * mm, "end": v(40.18, 1.75) * mm});
            skLineSegment(sketch, "E13.27.6", {"start": v(40.18, 1.58) * mm, "end": v(40.18, 1.76) * mm});
            skArc(sketch, "E13.27.7", {"start": v(39.8, 0.85) * mm, "mid": v(40.1, 1.16) * mm, "end": v(40.18, 1.58) * mm});
            skArc(sketch, "E13.27.8", {"start": v(38.25, 0.05) * mm, "mid": v(39.05, 0.42) * mm, "end": v(39.8, 0.85) * mm});
            skArc(sketch, "E13.27.9", {"start": v(37.94, 0) * mm, "mid": v(38.1, 0) * mm, "end": v(38.25, 0.05) * mm});
            skLineSegment(sketch, "E13.27.10", {"start": v(37.94, 0) * mm, "end": v(36.8, 0) * mm});
            skArc(sketch, "E13.27.11", {"start": v(36.8, 0) * mm, "mid": v(36.22, -0.24) * mm, "end": v(35.97, -0.81) * mm});
            skArc(sketch, "E13.28.0", {"start": v(34.54, 10.1) * mm, "mid": v(34.93, 9.6) * mm, "end": v(35.55, 9.53) * mm});
            skLineSegment(sketch, "E13.28.1", {"start": v(36.65, 9.83) * mm, "end": v(35.55, 9.53) * mm});
            skArc(sketch, "E13.28.2", {"start": v(36.96, 9.85) * mm, "mid": v(36.8, 9.85) * mm, "end": v(36.65, 9.83) * mm});
            skArc(sketch, "E13.28.3", {"start": v(36.96, 9.85) * mm, "mid": v(37.82, 9.7) * mm, "end": v(38.67, 9.48) * mm});
            skArc(sketch, "E13.28.4", {"start": v(39.22, 8.88) * mm, "mid": v(39.03, 9.25) * mm, "end": v(38.67, 9.48) * mm});
            skLineSegment(sketch, "E13.28.5", {"start": v(39.22, 8.88) * mm, "end": v(39.26, 8.7) * mm});
            skLineSegment(sketch, "E13.28.6", {"start": v(39.3, 8.53) * mm, "end": v(39.26, 8.7) * mm});
            skArc(sketch, "E13.28.7", {"start": v(39.05, 7.75) * mm, "mid": v(39.28, 8.1) * mm, "end": v(39.3, 8.53) * mm});
            skArc(sketch, "E13.28.8", {"start": v(37.66, 6.7) * mm, "mid": v(38.38, 7.2) * mm, "end": v(39.05, 7.75) * mm});
            skArc(sketch, "E13.28.9", {"start": v(37.37, 6.58) * mm, "mid": v(37.52, 6.62) * mm, "end": v(37.66, 6.7) * mm});
            skLineSegment(sketch, "E13.28.10", {"start": v(37.37, 6.58) * mm, "end": v(36.24, 6.39) * mm});
            skArc(sketch, "E13.28.11", {"start": v(36.24, 6.39) * mm, "mid": v(35.71, 6.06) * mm, "end": v(35.57, 5.45) * mm});
            skArc(sketch, "E13.29.0", {"start": v(32.26, 15.94) * mm, "mid": v(32.73, 15.52) * mm, "end": v(33.35, 15.56) * mm});
            skLineSegment(sketch, "E13.29.1", {"start": v(34.38, 16.04) * mm, "end": v(33.35, 15.56) * mm});
            skArc(sketch, "E13.29.2", {"start": v(34.7, 16.12) * mm, "mid": v(34.53, 16.1) * mm, "end": v(34.38, 16.04) * mm});
            skArc(sketch, "E13.29.3", {"start": v(34.7, 16.12) * mm, "mid": v(35.56, 16.13) * mm, "end": v(36.43, 16.05) * mm});
            skArc(sketch, "E13.29.4", {"start": v(37.09, 15.55) * mm, "mid": v(36.83, 15.89) * mm, "end": v(36.43, 16.05) * mm});
            skLineSegment(sketch, "E13.29.5", {"start": v(37.09, 15.55) * mm, "end": v(37.16, 15.39) * mm});
            skLineSegment(sketch, "E13.29.6", {"start": v(37.22, 15.23) * mm, "end": v(37.16, 15.4) * mm});
            skArc(sketch, "E13.29.7", {"start": v(37.11, 14.41) * mm, "mid": v(37.28, 14.8) * mm, "end": v(37.22, 15.23) * mm});
            skArc(sketch, "E13.29.8", {"start": v(35.93, 13.13) * mm, "mid": v(36.55, 13.75) * mm, "end": v(37.11, 14.41) * mm});
            skArc(sketch, "E13.29.9", {"start": v(35.66, 12.97) * mm, "mid": v(35.8, 13.04) * mm, "end": v(35.93, 13.13) * mm});
            skLineSegment(sketch, "E13.29.10", {"start": v(35.66, 12.97) * mm, "end": v(34.58, 12.58) * mm});
            skArc(sketch, "E13.29.11", {"start": v(34.58, 12.58) * mm, "mid": v(34.12, 12.17) * mm, "end": v(34.08, 11.54) * mm});
            skArc(sketch, "E13.30.0", {"start": v(29, 21.3) * mm, "mid": v(29.54, 20.97) * mm, "end": v(30.15, 21.11) * mm});
            skLineSegment(sketch, "E13.30.1", {"start": v(31.08, 21.77) * mm, "end": v(30.15, 21.11) * mm});
            skArc(sketch, "E13.30.2", {"start": v(31.37, 21.9) * mm, "mid": v(31.21, 21.85) * mm, "end": v(31.08, 21.77) * mm});
            skArc(sketch, "E13.30.3", {"start": v(31.37, 21.9) * mm, "mid": v(32.22, 22.06) * mm, "end": v(33.1, 22.13) * mm});
            skArc(sketch, "E13.30.4", {"start": v(33.82, 21.76) * mm, "mid": v(33.5, 22.04) * mm, "end": v(33.1, 22.13) * mm});
            skLineSegment(sketch, "E13.30.5", {"start": v(33.82, 21.76) * mm, "end": v(33.92, 21.6) * mm});
            skLineSegment(sketch, "E13.30.6", {"start": v(34.01, 21.46) * mm, "end": v(33.92, 21.6) * mm});
            skArc(sketch, "E13.30.7", {"start": v(34.05, 20.64) * mm, "mid": v(34.14, 21.05) * mm, "end": v(34.01, 21.46) * mm});
            skArc(sketch, "E13.30.8", {"start": v(33.1, 19.17) * mm, "mid": v(33.6, 19.88) * mm, "end": v(34.05, 20.64) * mm});
            skArc(sketch, "E13.30.9", {"start": v(32.86, 18.96) * mm, "mid": v(33, 19.06) * mm, "end": v(33.1, 19.17) * mm});
            skLineSegment(sketch, "E13.30.10", {"start": v(32.86, 18.96) * mm, "end": v(31.87, 18.4) * mm});
            skArc(sketch, "E13.30.11", {"start": v(31.87, 18.4) * mm, "mid": v(31.49, 17.9) * mm, "end": v(31.56, 17.29) * mm});
            skArc(sketch, "E13.31.0", {"start": v(24.86, 26.01) * mm, "mid": v(25.45, 25.78) * mm, "end": v(26.02, 26.03) * mm});
            skLineSegment(sketch, "E13.31.1", {"start": v(26.82, 26.83) * mm, "end": v(26.02, 26.03) * mm});
            skArc(sketch, "E13.31.2", {"start": v(27.09, 27.01) * mm, "mid": v(26.95, 26.94) * mm, "end": v(26.82, 26.83) * mm});
            skArc(sketch, "E13.31.3", {"start": v(27.09, 27.01) * mm, "mid": v(27.9, 27.32) * mm, "end": v(28.75, 27.54) * mm});
            skArc(sketch, "E13.31.4", {"start": v(29.53, 27.3) * mm, "mid": v(29.17, 27.53) * mm, "end": v(28.75, 27.54) * mm});
            skLineSegment(sketch, "E13.31.5", {"start": v(29.53, 27.3) * mm, "end": v(29.65, 27.17) * mm});
            skLineSegment(sketch, "E13.31.6", {"start": v(29.77, 27.04) * mm, "end": v(29.65, 27.17) * mm});
            skArc(sketch, "E13.31.7", {"start": v(29.94, 26.24) * mm, "mid": v(29.96, 26.66) * mm, "end": v(29.77, 27.04) * mm});
            skArc(sketch, "E13.31.8", {"start": v(29.27, 24.63) * mm, "mid": v(29.64, 25.42) * mm, "end": v(29.94, 26.24) * mm});
            skArc(sketch, "E13.31.9", {"start": v(29.07, 24.38) * mm, "mid": v(29.18, 24.5) * mm, "end": v(29.27, 24.63) * mm});
            skLineSegment(sketch, "E13.31.10", {"start": v(29.07, 24.38) * mm, "end": v(28.2, 23.65) * mm});
            skArc(sketch, "E13.31.11", {"start": v(28.2, 23.65) * mm, "mid": v(27.9, 23.1) * mm, "end": v(28.08, 22.5) * mm});
            skArc(sketch, "E13.32.0", {"start": v(19.97, 29.93) * mm, "mid": v(20.58, 29.8) * mm, "end": v(21.1, 30.15) * mm});
            skLineSegment(sketch, "E13.32.1", {"start": v(21.76, 31.08) * mm, "end": v(21.1, 30.15) * mm});
            skArc(sketch, "E13.32.2", {"start": v(21.98, 31.3) * mm, "mid": v(21.86, 31.2) * mm, "end": v(21.76, 31.08) * mm});
            skArc(sketch, "E13.32.3", {"start": v(21.98, 31.3) * mm, "mid": v(22.74, 31.75) * mm, "end": v(23.53, 32.12) * mm});
            skArc(sketch, "E13.32.4", {"start": v(24.34, 32.01) * mm, "mid": v(23.95, 32.17) * mm, "end": v(23.53, 32.12) * mm});
            skLineSegment(sketch, "E13.32.5", {"start": v(24.34, 32.01) * mm, "end": v(24.48, 31.9) * mm});
            skLineSegment(sketch, "E13.32.6", {"start": v(24.62, 31.8) * mm, "end": v(24.48, 31.9) * mm});
            skArc(sketch, "E13.32.7", {"start": v(24.93, 31.04) * mm, "mid": v(24.88, 31.46) * mm, "end": v(24.62, 31.8) * mm});
            skArc(sketch, "E13.32.8", {"start": v(24.55, 29.34) * mm, "mid": v(24.78, 30.18) * mm, "end": v(24.93, 31.04) * mm});
            skArc(sketch, "E13.32.9", {"start": v(24.4, 29.06) * mm, "mid": v(24.49, 29.2) * mm, "end": v(24.55, 29.34) * mm});
            skLineSegment(sketch, "E13.32.10", {"start": v(24.4, 29.06) * mm, "end": v(23.66, 28.2) * mm});
            skArc(sketch, "E13.32.11", {"start": v(23.66, 28.2) * mm, "mid": v(23.47, 27.6) * mm, "end": v(23.74, 27.04) * mm});
            skArc(sketch, "E13.33.0", {"start": v(14.47, 32.95) * mm, "mid": v(15.1, 32.93) * mm, "end": v(15.55, 33.36) * mm});
            skLineSegment(sketch, "E13.33.1", {"start": v(16.03, 34.4) * mm, "end": v(15.55, 33.36) * mm});
            skArc(sketch, "E13.33.2", {"start": v(16.21, 34.65) * mm, "mid": v(16.1, 34.53) * mm, "end": v(16.03, 34.4) * mm});
            skArc(sketch, "E13.33.3", {"start": v(16.21, 34.65) * mm, "mid": v(16.88, 35.21) * mm, "end": v(17.6, 35.71) * mm});
            skArc(sketch, "E13.33.4", {"start": v(18.41, 35.75) * mm, "mid": v(18, 35.84) * mm, "end": v(17.6, 35.71) * mm});
            skLineSegment(sketch, "E13.33.5", {"start": v(18.41, 35.75) * mm, "end": v(18.57, 35.67) * mm});
            skLineSegment(sketch, "E13.33.6", {"start": v(18.73, 35.59) * mm, "end": v(18.57, 35.67) * mm});
            skArc(sketch, "E13.33.7", {"start": v(19.16, 34.9) * mm, "mid": v(19.04, 35.3) * mm, "end": v(18.73, 35.59) * mm});
            skArc(sketch, "E13.33.8", {"start": v(19.08, 33.16) * mm, "mid": v(19.16, 34.02) * mm, "end": v(19.16, 34.9) * mm});
            skArc(sketch, "E13.33.9", {"start": v(18.98, 32.85) * mm, "mid": v(19.04, 33) * mm, "end": v(19.08, 33.16) * mm});
            skLineSegment(sketch, "E13.33.10", {"start": v(18.98, 32.85) * mm, "end": v(18.4, 31.87) * mm});
            skArc(sketch, "E13.33.11", {"start": v(18.4, 31.87) * mm, "mid": v(18.32, 31.25) * mm, "end": v(18.69, 30.75) * mm});
            skArc(sketch, "E13.34.0", {"start": v(8.53, 34.96) * mm, "mid": v(9.15, 35.05) * mm, "end": v(9.52, 35.55) * mm});
            skLineSegment(sketch, "E13.34.1", {"start": v(9.81, 36.65) * mm, "end": v(9.52, 35.55) * mm});
            skArc(sketch, "E13.34.2", {"start": v(9.95, 36.94) * mm, "mid": v(9.87, 36.8) * mm, "end": v(9.81, 36.65) * mm});
            skArc(sketch, "E13.34.3", {"start": v(9.95, 36.94) * mm, "mid": v(10.5, 37.6) * mm, "end": v(11.12, 38.23) * mm});
            skArc(sketch, "E13.34.4", {"start": v(11.92, 38.4) * mm, "mid": v(11.5, 38.42) * mm, "end": v(11.12, 38.23) * mm});
            skLineSegment(sketch, "E13.34.5", {"start": v(11.92, 38.4) * mm, "end": v(12.1, 38.36) * mm});
            skLineSegment(sketch, "E13.34.6", {"start": v(12.26, 38.3) * mm, "end": v(12.1, 38.36) * mm});
            skArc(sketch, "E13.34.7", {"start": v(12.81, 37.7) * mm, "mid": v(12.62, 38.07) * mm, "end": v(12.26, 38.3) * mm});
            skArc(sketch, "E13.34.8", {"start": v(13.03, 35.97) * mm, "mid": v(12.96, 36.83) * mm, "end": v(12.81, 37.7) * mm});
            skArc(sketch, "E13.34.9", {"start": v(12.98, 35.65) * mm, "mid": v(13.02, 35.8) * mm, "end": v(13.03, 35.97) * mm});
            skLineSegment(sketch, "E13.34.10", {"start": v(12.98, 35.65) * mm, "end": v(12.6, 34.58) * mm});
            skArc(sketch, "E13.34.11", {"start": v(12.6, 34.58) * mm, "mid": v(12.61, 33.96) * mm, "end": v(13.07, 33.53) * mm});
            skArc(sketch, "E13.35.0", {"start": v(2.33, 35.9) * mm, "mid": v(2.92, 36.1) * mm, "end": v(3.2, 36.66) * mm});
            skLineSegment(sketch, "E13.35.1", {"start": v(3.3, 37.8) * mm, "end": v(3.2, 36.66) * mm});
            skArc(sketch, "E13.35.2", {"start": v(3.39, 38.1) * mm, "mid": v(3.33, 37.96) * mm, "end": v(3.3, 37.8) * mm});
            skArc(sketch, "E13.35.3", {"start": v(3.39, 38.1) * mm, "mid": v(3.82, 38.86) * mm, "end": v(4.32, 39.58) * mm});
            skArc(sketch, "E13.35.4", {"start": v(5.07, 39.9) * mm, "mid": v(4.65, 39.84) * mm, "end": v(4.32, 39.58) * mm});
            skLineSegment(sketch, "E13.35.5", {"start": v(5.07, 39.9) * mm, "end": v(5.25, 39.87) * mm});
            skLineSegment(sketch, "E13.35.6", {"start": v(5.43, 39.85) * mm, "end": v(5.25, 39.87) * mm});
            skArc(sketch, "E13.35.7", {"start": v(6.07, 39.35) * mm, "mid": v(5.82, 39.68) * mm, "end": v(5.43, 39.85) * mm});
            skArc(sketch, "E13.35.8", {"start": v(6.6, 37.68) * mm, "mid": v(6.37, 38.53) * mm, "end": v(6.07, 39.35) * mm});
            skArc(sketch, "E13.35.9", {"start": v(6.6, 37.36) * mm, "mid": v(6.6, 37.52) * mm, "end": v(6.6, 37.68) * mm});
            skLineSegment(sketch, "E13.35.10", {"start": v(6.6, 37.36) * mm, "end": v(6.4, 36.24) * mm});
            skArc(sketch, "E13.35.11", {"start": v(6.4, 36.24) * mm, "mid": v(6.52, 35.63) * mm, "end": v(7.04, 35.29) * mm});
            skArc(sketch, "E14.trimOffspring", {"start": v(-15.94, 32.26) * mm, "mid": v(-16.62, 31.92) * mm, "end": v(-17.29, 31.56) * mm});
            skArc(sketch, "E15.trimOffspring", {"start": v(-10.1, 34.54) * mm, "mid": v(-10.82, 34.32) * mm, "end": v(-11.54, 34.08) * mm});
            skArc(sketch, "E16.trimOffspring", {"start": v(-29.93, 19.97) * mm, "mid": v(-30.35, 19.33) * mm, "end": v(-30.75, 18.69) * mm});
            skArc(sketch, "E17.trimOffspring", {"start": v(-32.95, 14.47) * mm, "mid": v(-33.24, 13.77) * mm, "end": v(-33.53, 13.07) * mm});
            skArc(sketch, "E18.trimOffspring", {"start": v(-34.96, 8.53) * mm, "mid": v(-35.13, 7.79) * mm, "end": v(-35.29, 7.04) * mm});
            skArc(sketch, "E19.trimOffspring", {"start": v(-35.9, 2.33) * mm, "mid": v(-35.95, 1.57) * mm, "end": v(-35.97, 0.81) * mm});
            skArc(sketch, "E20.trimOffspring", {"start": v(-35.77, -3.94) * mm, "mid": v(-35.68, -4.7) * mm, "end": v(-35.57, -5.45) * mm});
            skArc(sketch, "E21.trimOffspring", {"start": v(-34.54, -10.1) * mm, "mid": v(-34.32, -10.82) * mm, "end": v(-34.08, -11.54) * mm});
            skArc(sketch, "E22.trimOffspring", {"start": v(-32.26, -15.94) * mm, "mid": v(-31.92, -16.62) * mm, "end": v(-31.56, -17.29) * mm});
            skArc(sketch, "E23.trimOffspring", {"start": v(-29, -21.3) * mm, "mid": v(-28.55, -21.9) * mm, "end": v(-28.08, -22.5) * mm});
            skArc(sketch, "E24.trimOffspring", {"start": v(-24.86, -26.01) * mm, "mid": v(-24.3, -26.53) * mm, "end": v(-23.74, -27.04) * mm});
            skArc(sketch, "E25.trimOffspring", {"start": v(-19.97, -29.93) * mm, "mid": v(-19.33, -30.35) * mm, "end": v(-18.69, -30.75) * mm});
            skArc(sketch, "E26.trimOffspring", {"start": v(-14.47, -32.95) * mm, "mid": v(-13.77, -33.24) * mm, "end": v(-13.07, -33.53) * mm});
            skArc(sketch, "E27.trimOffspring", {"start": v(-8.53, -34.96) * mm, "mid": v(-7.79, -35.13) * mm, "end": v(-7.04, -35.29) * mm});
            skArc(sketch, "E28.trimOffspring", {"start": v(-2.33, -35.9) * mm, "mid": v(-1.57, -35.95) * mm, "end": v(-0.81, -35.97) * mm});
            skArc(sketch, "E29.trimOffspring", {"start": v(3.94, -35.77) * mm, "mid": v(4.7, -35.68) * mm, "end": v(5.45, -35.57) * mm});
            skArc(sketch, "E30.trimOffspring", {"start": v(10.1, -34.54) * mm, "mid": v(10.82, -34.32) * mm, "end": v(11.54, -34.08) * mm});
            skArc(sketch, "E31.trimOffspring", {"start": v(15.94, -32.26) * mm, "mid": v(16.62, -31.92) * mm, "end": v(17.29, -31.56) * mm});
            skArc(sketch, "E32.trimOffspring", {"start": v(21.3, -29) * mm, "mid": v(21.9, -28.55) * mm, "end": v(22.5, -28.08) * mm});
            skArc(sketch, "E33.trimOffspring", {"start": v(26.01, -24.86) * mm, "mid": v(26.53, -24.3) * mm, "end": v(27.04, -23.74) * mm});
            skArc(sketch, "E34.trimOffspring", {"start": v(29.93, -19.97) * mm, "mid": v(30.35, -19.33) * mm, "end": v(30.75, -18.69) * mm});
            skArc(sketch, "E35.trimOffspring", {"start": v(32.95, -14.47) * mm, "mid": v(33.24, -13.77) * mm, "end": v(33.53, -13.07) * mm});
            skArc(sketch, "E36.trimOffspring", {"start": v(34.96, -8.53) * mm, "mid": v(35.13, -7.79) * mm, "end": v(35.29, -7.04) * mm});
            skArc(sketch, "E37.trimOffspring", {"start": v(35.9, -2.33) * mm, "mid": v(35.95, -1.57) * mm, "end": v(35.97, -0.81) * mm});
            skArc(sketch, "E38.trimOffspring", {"start": v(35.77, 3.94) * mm, "mid": v(35.68, 4.7) * mm, "end": v(35.57, 5.45) * mm});
            skArc(sketch, "E39.trimOffspring", {"start": v(34.54, 10.1) * mm, "mid": v(34.32, 10.82) * mm, "end": v(34.08, 11.54) * mm});
            skArc(sketch, "E40.trimOffspring", {"start": v(32.26, 15.94) * mm, "mid": v(31.92, 16.62) * mm, "end": v(31.56, 17.29) * mm});
            skArc(sketch, "E41.trimOffspring", {"start": v(29, 21.3) * mm, "mid": v(28.55, 21.9) * mm, "end": v(28.08, 22.5) * mm});
            skArc(sketch, "E42.trimOffspring", {"start": v(24.86, 26.01) * mm, "mid": v(24.3, 26.53) * mm, "end": v(23.74, 27.04) * mm});
            skArc(sketch, "E43.trimOffspring", {"start": v(19.97, 29.93) * mm, "mid": v(19.33, 30.35) * mm, "end": v(18.69, 30.75) * mm});
            skArc(sketch, "E44.trimOffspring", {"start": v(14.47, 32.95) * mm, "mid": v(13.77, 33.24) * mm, "end": v(13.07, 33.53) * mm});
            skArc(sketch, "E45.trimOffspring", {"start": v(8.53, 34.96) * mm, "mid": v(7.79, 35.13) * mm, "end": v(7.04, 35.29) * mm});
            skArc(sketch, "E46.trimOffspring", {"start": v(2.33, 35.9) * mm, "mid": v(1.57, 35.95) * mm, "end": v(0.81, 35.97) * mm});
            skArc(sketch, "E47.trimOffspring", {"start": v(-21.3, 29) * mm, "mid": v(-21.9, 28.55) * mm, "end": v(-22.5, 28.08) * mm});
            skArc(sketch, "E48.trimOffspring", {"start": v(-26.01, 24.86) * mm, "mid": v(-26.53, 24.3) * mm, "end": v(-27.04, 23.74) * mm});
            skSolve(sketch);
        }
        {
            var Q0;
            Q0=makeQuery(id+"F0.imprint","IMPRINT",FACE,{"disambiguationData":[TD([[makeQuery(id+"F0.imprint","IMPRINT",EDGE,{"derivedFrom":sQuery(id+"F0.wireOp",EDGE,"E0")}),1.0]])]});
            extrude(context, id + "F1", {"entities" : qUnion([Q0]), "depth" : 12.7 * mm});
        }
        {
            var Q0;
            Q0=makeQuery(id+"F1.opExtrude","CAP_FACE",FACE,{"disambiguationData":[OSD([sQuery(id+"F0.wireOp",EDGE,"E0"),sQuery(id+"F0.wireOp",EDGE,"E1"),sQuery(id+"F0.wireOp",EDGE,"E2"),sQuery(id+"F0.wireOp",EDGE,"E3"),sQuery(id+"F0.wireOp",EDGE,"E4.MirrorCS"),sQuery(id+"F0.wireOp",EDGE,"E5.MirrorCS"),sQuery(id+"F0.wireOp",EDGE,"E6.MirrorCS"),sQuery(id+"F0.wireOp",EDGE,"E7.filletArc"),sQuery(id+"F0.wireOp",EDGE,"E8.filletArc"),sQuery(id+"F0.wireOp",EDGE,"E9.filletArc"),sQuery(id+"F0.wireOp",EDGE,"E10.filletArc"),sQuery(id+"F0.wireOp",EDGE,"E11.filletArc"),sQuery(id+"F0.wireOp",EDGE,"E12.filletArc"),sQuery(id+"F0.wireOp",EDGE,"E13.1.0"),sQuery(id+"F0.wireOp",EDGE,"E13.1.1"),sQuery(id+"F0.wireOp",EDGE,"E13.1.2"),sQuery(id+"F0.wireOp",EDGE,"E13.1.3"),sQuery(id+"F0.wireOp",EDGE,"E13.1.4"),sQuery(id+"F0.wireOp",EDGE,"E13.1.5"),sQuery(id+"F0.wireOp",EDGE,"E13.1.6"),sQuery(id+"F0.wireOp",EDGE,"E13.1.7"),sQuery(id+"F0.wireOp",EDGE,"E13.1.8"),sQuery(id+"F0.wireOp",EDGE,"E13.1.9"),sQuery(id+"F0.wireOp",EDGE,"E13.1.10"),sQuery(id+"F0.wireOp",EDGE,"E13.1.11"),sQuery(id+"F0.wireOp",EDGE,"E13.2.0"),sQuery(id+"F0.wireOp",EDGE,"E13.2.1"),sQuery(id+"F0.wireOp",EDGE,"E13.2.2"),sQuery(id+"F0.wireOp",EDGE,"E13.2.3"),sQuery(id+"F0.wireOp",EDGE,"E13.2.4"),sQuery(id+"F0.wireOp",EDGE,"E13.2.5"),sQuery(id+"F0.wireOp",EDGE,"E13.2.6"),sQuery(id+"F0.wireOp",EDGE,"E13.2.7"),sQuery(id+"F0.wireOp",EDGE,"E13.2.8"),sQuery(id+"F0.wireOp",EDGE,"E13.2.9"),sQuery(id+"F0.wireOp",EDGE,"E13.2.10"),sQuery(id+"F0.wireOp",EDGE,"E13.2.11"),sQuery(id+"F0.wireOp",EDGE,"E13.3.0"),sQuery(id+"F0.wireOp",EDGE,"E13.3.1"),sQuery(id+"F0.wireOp",EDGE,"E13.3.2"),sQuery(id+"F0.wireOp",EDGE,"E13.3.3"),sQuery(id+"F0.wireOp",EDGE,"E13.3.4"),sQuery(id+"F0.wireOp",EDGE,"E13.3.5"),sQuery(id+"F0.wireOp",EDGE,"E13.3.6"),sQuery(id+"F0.wireOp",EDGE,"E13.3.7"),sQuery(id+"F0.wireOp",EDGE,"E13.3.8"),sQuery(id+"F0.wireOp",EDGE,"E13.3.9"),sQuery(id+"F0.wireOp",EDGE,"E13.3.10"),sQuery(id+"F0.wireOp",EDGE,"E13.3.11"),sQuery(id+"F0.wireOp",EDGE,"E13.4.0"),sQuery(id+"F0.wireOp",EDGE,"E13.4.1"),sQuery(id+"F0.wireOp",EDGE,"E13.4.2"),sQuery(id+"F0.wireOp",EDGE,"E13.4.3"),sQuery(id+"F0.wireOp",EDGE,"E13.4.4"),sQuery(id+"F0.wireOp",EDGE,"E13.4.5"),sQuery(id+"F0.wireOp",EDGE,"E13.4.6"),sQuery(id+"F0.wireOp",EDGE,"E13.4.7"),sQuery(id+"F0.wireOp",EDGE,"E13.4.8"),sQuery(id+"F0.wireOp",EDGE,"E13.4.9"),sQuery(id+"F0.wireOp",EDGE,"E13.4.10"),sQuery(id+"F0.wireOp",EDGE,"E13.4.11"),sQuery(id+"F0.wireOp",EDGE,"E13.5.0"),sQuery(id+"F0.wireOp",EDGE,"E13.5.1"),sQuery(id+"F0.wireOp",EDGE,"E13.5.2"),sQuery(id+"F0.wireOp",EDGE,"E13.5.3"),sQuery(id+"F0.wireOp",EDGE,"E13.5.4"),sQuery(id+"F0.wireOp",EDGE,"E13.5.5"),sQuery(id+"F0.wireOp",EDGE,"E13.5.6"),sQuery(id+"F0.wireOp",EDGE,"E13.5.7"),sQuery(id+"F0.wireOp",EDGE,"E13.5.8"),sQuery(id+"F0.wireOp",EDGE,"E13.5.9"),sQuery(id+"F0.wireOp",EDGE,"E13.5.10"),sQuery(id+"F0.wireOp",EDGE,"E13.5.11"),sQuery(id+"F0.wireOp",EDGE,"E13.6.0"),sQuery(id+"F0.wireOp",EDGE,"E13.6.1"),sQuery(id+"F0.wireOp",EDGE,"E13.6.2"),sQuery(id+"F0.wireOp",EDGE,"E13.6.3"),sQuery(id+"F0.wireOp",EDGE,"E13.6.4"),sQuery(id+"F0.wireOp",EDGE,"E13.6.5"),sQuery(id+"F0.wireOp",EDGE,"E13.6.6"),sQuery(id+"F0.wireOp",EDGE,"E13.6.7"),sQuery(id+"F0.wireOp",EDGE,"E13.6.8"),sQuery(id+"F0.wireOp",EDGE,"E13.6.9"),sQuery(id+"F0.wireOp",EDGE,"E13.6.10"),sQuery(id+"F0.wireOp",EDGE,"E13.6.11"),sQuery(id+"F0.wireOp",EDGE,"E13.7.0"),sQuery(id+"F0.wireOp",EDGE,"E13.7.1"),sQuery(id+"F0.wireOp",EDGE,"E13.7.2"),sQuery(id+"F0.wireOp",EDGE,"E13.7.3"),sQuery(id+"F0.wireOp",EDGE,"E13.7.4"),sQuery(id+"F0.wireOp",EDGE,"E13.7.5"),sQuery(id+"F0.wireOp",EDGE,"E13.7.6"),sQuery(id+"F0.wireOp",EDGE,"E13.7.7"),sQuery(id+"F0.wireOp",EDGE,"E13.7.8"),sQuery(id+"F0.wireOp",EDGE,"E13.7.9"),sQuery(id+"F0.wireOp",EDGE,"E13.7.10"),sQuery(id+"F0.wireOp",EDGE,"E13.7.11"),sQuery(id+"F0.wireOp",EDGE,"E13.8.0"),sQuery(id+"F0.wireOp",EDGE,"E13.8.1"),sQuery(id+"F0.wireOp",EDGE,"E13.8.2"),sQuery(id+"F0.wireOp",EDGE,"E13.8.3"),sQuery(id+"F0.wireOp",EDGE,"E13.8.4"),sQuery(id+"F0.wireOp",EDGE,"E13.8.5"),sQuery(id+"F0.wireOp",EDGE,"E13.8.6"),sQuery(id+"F0.wireOp",EDGE,"E13.8.7"),sQuery(id+"F0.wireOp",EDGE,"E13.8.8"),sQuery(id+"F0.wireOp",EDGE,"E13.8.9"),sQuery(id+"F0.wireOp",EDGE,"E13.8.10"),sQuery(id+"F0.wireOp",EDGE,"E13.8.11"),sQuery(id+"F0.wireOp",EDGE,"E13.9.0"),sQuery(id+"F0.wireOp",EDGE,"E13.9.1"),sQuery(id+"F0.wireOp",EDGE,"E13.9.2"),sQuery(id+"F0.wireOp",EDGE,"E13.9.3"),sQuery(id+"F0.wireOp",EDGE,"E13.9.4"),sQuery(id+"F0.wireOp",EDGE,"E13.9.5"),sQuery(id+"F0.wireOp",EDGE,"E13.9.6"),sQuery(id+"F0.wireOp",EDGE,"E13.9.7"),sQuery(id+"F0.wireOp",EDGE,"E13.9.8"),sQuery(id+"F0.wireOp",EDGE,"E13.9.9"),sQuery(id+"F0.wireOp",EDGE,"E13.9.10"),sQuery(id+"F0.wireOp",EDGE,"E13.9.11"),sQuery(id+"F0.wireOp",EDGE,"E13.10.0"),sQuery(id+"F0.wireOp",EDGE,"E13.10.1"),sQuery(id+"F0.wireOp",EDGE,"E13.10.2"),sQuery(id+"F0.wireOp",EDGE,"E13.10.3"),sQuery(id+"F0.wireOp",EDGE,"E13.10.4"),sQuery(id+"F0.wireOp",EDGE,"E13.10.5"),sQuery(id+"F0.wireOp",EDGE,"E13.10.6"),sQuery(id+"F0.wireOp",EDGE,"E13.10.7"),sQuery(id+"F0.wireOp",EDGE,"E13.10.8"),sQuery(id+"F0.wireOp",EDGE,"E13.10.9"),sQuery(id+"F0.wireOp",EDGE,"E13.10.10"),sQuery(id+"F0.wireOp",EDGE,"E13.10.11"),sQuery(id+"F0.wireOp",EDGE,"E13.11.0"),sQuery(id+"F0.wireOp",EDGE,"E13.11.1"),sQuery(id+"F0.wireOp",EDGE,"E13.11.2"),sQuery(id+"F0.wireOp",EDGE,"E13.11.3"),sQuery(id+"F0.wireOp",EDGE,"E13.11.4"),sQuery(id+"F0.wireOp",EDGE,"E13.11.5"),sQuery(id+"F0.wireOp",EDGE,"E13.11.6"),sQuery(id+"F0.wireOp",EDGE,"E13.11.7"),sQuery(id+"F0.wireOp",EDGE,"E13.11.8"),sQuery(id+"F0.wireOp",EDGE,"E13.11.9"),sQuery(id+"F0.wireOp",EDGE,"E13.11.10"),sQuery(id+"F0.wireOp",EDGE,"E13.11.11"),sQuery(id+"F0.wireOp",EDGE,"E13.12.0"),sQuery(id+"F0.wireOp",EDGE,"E13.12.1"),sQuery(id+"F0.wireOp",EDGE,"E13.12.2"),sQuery(id+"F0.wireOp",EDGE,"E13.12.3"),sQuery(id+"F0.wireOp",EDGE,"E13.12.4"),sQuery(id+"F0.wireOp",EDGE,"E13.12.5"),sQuery(id+"F0.wireOp",EDGE,"E13.12.6"),sQuery(id+"F0.wireOp",EDGE,"E13.12.7"),sQuery(id+"F0.wireOp",EDGE,"E13.12.8"),sQuery(id+"F0.wireOp",EDGE,"E13.12.9"),sQuery(id+"F0.wireOp",EDGE,"E13.12.10"),sQuery(id+"F0.wireOp",EDGE,"E13.12.11"),sQuery(id+"F0.wireOp",EDGE,"E13.13.0"),sQuery(id+"F0.wireOp",EDGE,"E13.13.1"),sQuery(id+"F0.wireOp",EDGE,"E13.13.2"),sQuery(id+"F0.wireOp",EDGE,"E13.13.3"),sQuery(id+"F0.wireOp",EDGE,"E13.13.4"),sQuery(id+"F0.wireOp",EDGE,"E13.13.5"),sQuery(id+"F0.wireOp",EDGE,"E13.13.6"),sQuery(id+"F0.wireOp",EDGE,"E13.13.7"),sQuery(id+"F0.wireOp",EDGE,"E13.13.8"),sQuery(id+"F0.wireOp",EDGE,"E13.13.9"),sQuery(id+"F0.wireOp",EDGE,"E13.13.10"),sQuery(id+"F0.wireOp",EDGE,"E13.13.11"),sQuery(id+"F0.wireOp",EDGE,"E13.14.0"),sQuery(id+"F0.wireOp",EDGE,"E13.14.1"),sQuery(id+"F0.wireOp",EDGE,"E13.14.2"),sQuery(id+"F0.wireOp",EDGE,"E13.14.3"),sQuery(id+"F0.wireOp",EDGE,"E13.14.4"),sQuery(id+"F0.wireOp",EDGE,"E13.14.5"),sQuery(id+"F0.wireOp",EDGE,"E13.14.6"),sQuery(id+"F0.wireOp",EDGE,"E13.14.7"),sQuery(id+"F0.wireOp",EDGE,"E13.14.8"),sQuery(id+"F0.wireOp",EDGE,"E13.14.9"),sQuery(id+"F0.wireOp",EDGE,"E13.14.10"),sQuery(id+"F0.wireOp",EDGE,"E13.14.11"),sQuery(id+"F0.wireOp",EDGE,"E13.15.0"),sQuery(id+"F0.wireOp",EDGE,"E13.15.1"),sQuery(id+"F0.wireOp",EDGE,"E13.15.2"),sQuery(id+"F0.wireOp",EDGE,"E13.15.3"),sQuery(id+"F0.wireOp",EDGE,"E13.15.4"),sQuery(id+"F0.wireOp",EDGE,"E13.15.5"),sQuery(id+"F0.wireOp",EDGE,"E13.15.6"),sQuery(id+"F0.wireOp",EDGE,"E13.15.7"),sQuery(id+"F0.wireOp",EDGE,"E13.15.8"),sQuery(id+"F0.wireOp",EDGE,"E13.15.9"),sQuery(id+"F0.wireOp",EDGE,"E13.15.10"),sQuery(id+"F0.wireOp",EDGE,"E13.15.11"),sQuery(id+"F0.wireOp",EDGE,"E13.16.0"),sQuery(id+"F0.wireOp",EDGE,"E13.16.1"),sQuery(id+"F0.wireOp",EDGE,"E13.16.2"),sQuery(id+"F0.wireOp",EDGE,"E13.16.3"),sQuery(id+"F0.wireOp",EDGE,"E13.16.4"),sQuery(id+"F0.wireOp",EDGE,"E13.16.5"),sQuery(id+"F0.wireOp",EDGE,"E13.16.6"),sQuery(id+"F0.wireOp",EDGE,"E13.16.7"),sQuery(id+"F0.wireOp",EDGE,"E13.16.8"),sQuery(id+"F0.wireOp",EDGE,"E13.16.9"),sQuery(id+"F0.wireOp",EDGE,"E13.16.10"),sQuery(id+"F0.wireOp",EDGE,"E13.16.11"),sQuery(id+"F0.wireOp",EDGE,"E13.17.0"),sQuery(id+"F0.wireOp",EDGE,"E13.17.1"),sQuery(id+"F0.wireOp",EDGE,"E13.17.2"),sQuery(id+"F0.wireOp",EDGE,"E13.17.3"),sQuery(id+"F0.wireOp",EDGE,"E13.17.4"),sQuery(id+"F0.wireOp",EDGE,"E13.17.5"),sQuery(id+"F0.wireOp",EDGE,"E13.17.6"),sQuery(id+"F0.wireOp",EDGE,"E13.17.7"),sQuery(id+"F0.wireOp",EDGE,"E13.17.8"),sQuery(id+"F0.wireOp",EDGE,"E13.17.9"),sQuery(id+"F0.wireOp",EDGE,"E13.17.10"),sQuery(id+"F0.wireOp",EDGE,"E13.17.11"),sQuery(id+"F0.wireOp",EDGE,"E13.18.0"),sQuery(id+"F0.wireOp",EDGE,"E13.18.1"),sQuery(id+"F0.wireOp",EDGE,"E13.18.2"),sQuery(id+"F0.wireOp",EDGE,"E13.18.3"),sQuery(id+"F0.wireOp",EDGE,"E13.18.4"),sQuery(id+"F0.wireOp",EDGE,"E13.18.5"),sQuery(id+"F0.wireOp",EDGE,"E13.18.6"),sQuery(id+"F0.wireOp",EDGE,"E13.18.7"),sQuery(id+"F0.wireOp",EDGE,"E13.18.8"),sQuery(id+"F0.wireOp",EDGE,"E13.18.9"),sQuery(id+"F0.wireOp",EDGE,"E13.18.10"),sQuery(id+"F0.wireOp",EDGE,"E13.18.11"),sQuery(id+"F0.wireOp",EDGE,"E13.19.0"),sQuery(id+"F0.wireOp",EDGE,"E13.19.1"),sQuery(id+"F0.wireOp",EDGE,"E13.19.2"),sQuery(id+"F0.wireOp",EDGE,"E13.19.3"),sQuery(id+"F0.wireOp",EDGE,"E13.19.4"),sQuery(id+"F0.wireOp",EDGE,"E13.19.5"),sQuery(id+"F0.wireOp",EDGE,"E13.19.6"),sQuery(id+"F0.wireOp",EDGE,"E13.19.7"),sQuery(id+"F0.wireOp",EDGE,"E13.19.8"),sQuery(id+"F0.wireOp",EDGE,"E13.19.9"),sQuery(id+"F0.wireOp",EDGE,"E13.19.10"),sQuery(id+"F0.wireOp",EDGE,"E13.19.11"),sQuery(id+"F0.wireOp",EDGE,"E13.20.0"),sQuery(id+"F0.wireOp",EDGE,"E13.20.1"),sQuery(id+"F0.wireOp",EDGE,"E13.20.2"),sQuery(id+"F0.wireOp",EDGE,"E13.20.3"),sQuery(id+"F0.wireOp",EDGE,"E13.20.4"),sQuery(id+"F0.wireOp",EDGE,"E13.20.5"),sQuery(id+"F0.wireOp",EDGE,"E13.20.6"),sQuery(id+"F0.wireOp",EDGE,"E13.20.7"),sQuery(id+"F0.wireOp",EDGE,"E13.20.8"),sQuery(id+"F0.wireOp",EDGE,"E13.20.9"),sQuery(id+"F0.wireOp",EDGE,"E13.20.10"),sQuery(id+"F0.wireOp",EDGE,"E13.20.11"),sQuery(id+"F0.wireOp",EDGE,"E13.21.0"),sQuery(id+"F0.wireOp",EDGE,"E13.21.1"),sQuery(id+"F0.wireOp",EDGE,"E13.21.2"),sQuery(id+"F0.wireOp",EDGE,"E13.21.3"),sQuery(id+"F0.wireOp",EDGE,"E13.21.4"),sQuery(id+"F0.wireOp",EDGE,"E13.21.5"),sQuery(id+"F0.wireOp",EDGE,"E13.21.6"),sQuery(id+"F0.wireOp",EDGE,"E13.21.7"),sQuery(id+"F0.wireOp",EDGE,"E13.21.8"),sQuery(id+"F0.wireOp",EDGE,"E13.21.9"),sQuery(id+"F0.wireOp",EDGE,"E13.21.10"),sQuery(id+"F0.wireOp",EDGE,"E13.21.11"),sQuery(id+"F0.wireOp",EDGE,"E13.22.0"),sQuery(id+"F0.wireOp",EDGE,"E13.22.1"),sQuery(id+"F0.wireOp",EDGE,"E13.22.2"),sQuery(id+"F0.wireOp",EDGE,"E13.22.3"),sQuery(id+"F0.wireOp",EDGE,"E13.22.4"),sQuery(id+"F0.wireOp",EDGE,"E13.22.5"),sQuery(id+"F0.wireOp",EDGE,"E13.22.6"),sQuery(id+"F0.wireOp",EDGE,"E13.22.7"),sQuery(id+"F0.wireOp",EDGE,"E13.22.8"),sQuery(id+"F0.wireOp",EDGE,"E13.22.9"),sQuery(id+"F0.wireOp",EDGE,"E13.22.10"),sQuery(id+"F0.wireOp",EDGE,"E13.22.11"),sQuery(id+"F0.wireOp",EDGE,"E13.23.0"),sQuery(id+"F0.wireOp",EDGE,"E13.23.1"),sQuery(id+"F0.wireOp",EDGE,"E13.23.2"),sQuery(id+"F0.wireOp",EDGE,"E13.23.3"),sQuery(id+"F0.wireOp",EDGE,"E13.23.4"),sQuery(id+"F0.wireOp",EDGE,"E13.23.5"),sQuery(id+"F0.wireOp",EDGE,"E13.23.6"),sQuery(id+"F0.wireOp",EDGE,"E13.23.7"),sQuery(id+"F0.wireOp",EDGE,"E13.23.8"),sQuery(id+"F0.wireOp",EDGE,"E13.23.9"),sQuery(id+"F0.wireOp",EDGE,"E13.23.10"),sQuery(id+"F0.wireOp",EDGE,"E13.23.11"),sQuery(id+"F0.wireOp",EDGE,"E13.24.0"),sQuery(id+"F0.wireOp",EDGE,"E13.24.1"),sQuery(id+"F0.wireOp",EDGE,"E13.24.2"),sQuery(id+"F0.wireOp",EDGE,"E13.24.3"),sQuery(id+"F0.wireOp",EDGE,"E13.24.4"),sQuery(id+"F0.wireOp",EDGE,"E13.24.5"),sQuery(id+"F0.wireOp",EDGE,"E13.24.6"),sQuery(id+"F0.wireOp",EDGE,"E13.24.7"),sQuery(id+"F0.wireOp",EDGE,"E13.24.8"),sQuery(id+"F0.wireOp",EDGE,"E13.24.9"),sQuery(id+"F0.wireOp",EDGE,"E13.24.10"),sQuery(id+"F0.wireOp",EDGE,"E13.24.11"),sQuery(id+"F0.wireOp",EDGE,"E13.25.0"),sQuery(id+"F0.wireOp",EDGE,"E13.25.1"),sQuery(id+"F0.wireOp",EDGE,"E13.25.2"),sQuery(id+"F0.wireOp",EDGE,"E13.25.3"),sQuery(id+"F0.wireOp",EDGE,"E13.25.4"),sQuery(id+"F0.wireOp",EDGE,"E13.25.5"),sQuery(id+"F0.wireOp",EDGE,"E13.25.6"),sQuery(id+"F0.wireOp",EDGE,"E13.25.7"),sQuery(id+"F0.wireOp",EDGE,"E13.25.8"),sQuery(id+"F0.wireOp",EDGE,"E13.25.9"),sQuery(id+"F0.wireOp",EDGE,"E13.25.10"),sQuery(id+"F0.wireOp",EDGE,"E13.25.11"),sQuery(id+"F0.wireOp",EDGE,"E13.26.0"),sQuery(id+"F0.wireOp",EDGE,"E13.26.1"),sQuery(id+"F0.wireOp",EDGE,"E13.26.2"),sQuery(id+"F0.wireOp",EDGE,"E13.26.3"),sQuery(id+"F0.wireOp",EDGE,"E13.26.4"),sQuery(id+"F0.wireOp",EDGE,"E13.26.5"),sQuery(id+"F0.wireOp",EDGE,"E13.26.6"),sQuery(id+"F0.wireOp",EDGE,"E13.26.7"),sQuery(id+"F0.wireOp",EDGE,"E13.26.8"),sQuery(id+"F0.wireOp",EDGE,"E13.26.9"),sQuery(id+"F0.wireOp",EDGE,"E13.26.10"),sQuery(id+"F0.wireOp",EDGE,"E13.26.11"),sQuery(id+"F0.wireOp",EDGE,"E13.27.0"),sQuery(id+"F0.wireOp",EDGE,"E13.27.1"),sQuery(id+"F0.wireOp",EDGE,"E13.27.2"),sQuery(id+"F0.wireOp",EDGE,"E13.27.3"),sQuery(id+"F0.wireOp",EDGE,"E13.27.4"),sQuery(id+"F0.wireOp",EDGE,"E13.27.5"),sQuery(id+"F0.wireOp",EDGE,"E13.27.6"),sQuery(id+"F0.wireOp",EDGE,"E13.27.7"),sQuery(id+"F0.wireOp",EDGE,"E13.27.8"),sQuery(id+"F0.wireOp",EDGE,"E13.27.9"),sQuery(id+"F0.wireOp",EDGE,"E13.27.10"),sQuery(id+"F0.wireOp",EDGE,"E13.27.11"),sQuery(id+"F0.wireOp",EDGE,"E13.28.0"),sQuery(id+"F0.wireOp",EDGE,"E13.28.1"),sQuery(id+"F0.wireOp",EDGE,"E13.28.2"),sQuery(id+"F0.wireOp",EDGE,"E13.28.3"),sQuery(id+"F0.wireOp",EDGE,"E13.28.4"),sQuery(id+"F0.wireOp",EDGE,"E13.28.5"),sQuery(id+"F0.wireOp",EDGE,"E13.28.6"),sQuery(id+"F0.wireOp",EDGE,"E13.28.7"),sQuery(id+"F0.wireOp",EDGE,"E13.28.8"),sQuery(id+"F0.wireOp",EDGE,"E13.28.9"),sQuery(id+"F0.wireOp",EDGE,"E13.28.10"),sQuery(id+"F0.wireOp",EDGE,"E13.28.11"),sQuery(id+"F0.wireOp",EDGE,"E13.29.0"),sQuery(id+"F0.wireOp",EDGE,"E13.29.1"),sQuery(id+"F0.wireOp",EDGE,"E13.29.2"),sQuery(id+"F0.wireOp",EDGE,"E13.29.3"),sQuery(id+"F0.wireOp",EDGE,"E13.29.4"),sQuery(id+"F0.wireOp",EDGE,"E13.29.5"),sQuery(id+"F0.wireOp",EDGE,"E13.29.6"),sQuery(id+"F0.wireOp",EDGE,"E13.29.7"),sQuery(id+"F0.wireOp",EDGE,"E13.29.8"),sQuery(id+"F0.wireOp",EDGE,"E13.29.9"),sQuery(id+"F0.wireOp",EDGE,"E13.29.10"),sQuery(id+"F0.wireOp",EDGE,"E13.29.11"),sQuery(id+"F0.wireOp",EDGE,"E13.30.0"),sQuery(id+"F0.wireOp",EDGE,"E13.30.1"),sQuery(id+"F0.wireOp",EDGE,"E13.30.2"),sQuery(id+"F0.wireOp",EDGE,"E13.30.3"),sQuery(id+"F0.wireOp",EDGE,"E13.30.4"),sQuery(id+"F0.wireOp",EDGE,"E13.30.5"),sQuery(id+"F0.wireOp",EDGE,"E13.30.6"),sQuery(id+"F0.wireOp",EDGE,"E13.30.7"),sQuery(id+"F0.wireOp",EDGE,"E13.30.8"),sQuery(id+"F0.wireOp",EDGE,"E13.30.9"),sQuery(id+"F0.wireOp",EDGE,"E13.30.10"),sQuery(id+"F0.wireOp",EDGE,"E13.30.11"),sQuery(id+"F0.wireOp",EDGE,"E13.31.0"),sQuery(id+"F0.wireOp",EDGE,"E13.31.1"),sQuery(id+"F0.wireOp",EDGE,"E13.31.2"),sQuery(id+"F0.wireOp",EDGE,"E13.31.3"),sQuery(id+"F0.wireOp",EDGE,"E13.31.4"),sQuery(id+"F0.wireOp",EDGE,"E13.31.5"),sQuery(id+"F0.wireOp",EDGE,"E13.31.6"),sQuery(id+"F0.wireOp",EDGE,"E13.31.7"),sQuery(id+"F0.wireOp",EDGE,"E13.31.8"),sQuery(id+"F0.wireOp",EDGE,"E13.31.9"),sQuery(id+"F0.wireOp",EDGE,"E13.31.10"),sQuery(id+"F0.wireOp",EDGE,"E13.31.11"),sQuery(id+"F0.wireOp",EDGE,"E13.32.0"),sQuery(id+"F0.wireOp",EDGE,"E13.32.1"),sQuery(id+"F0.wireOp",EDGE,"E13.32.2"),sQuery(id+"F0.wireOp",EDGE,"E13.32.3"),sQuery(id+"F0.wireOp",EDGE,"E13.32.4"),sQuery(id+"F0.wireOp",EDGE,"E13.32.5"),sQuery(id+"F0.wireOp",EDGE,"E13.32.6"),sQuery(id+"F0.wireOp",EDGE,"E13.32.7"),sQuery(id+"F0.wireOp",EDGE,"E13.32.8"),sQuery(id+"F0.wireOp",EDGE,"E13.32.9"),sQuery(id+"F0.wireOp",EDGE,"E13.32.10"),sQuery(id+"F0.wireOp",EDGE,"E13.32.11"),sQuery(id+"F0.wireOp",EDGE,"E13.33.0"),sQuery(id+"F0.wireOp",EDGE,"E13.33.1"),sQuery(id+"F0.wireOp",EDGE,"E13.33.2"),sQuery(id+"F0.wireOp",EDGE,"E13.33.3"),sQuery(id+"F0.wireOp",EDGE,"E13.33.4"),sQuery(id+"F0.wireOp",EDGE,"E13.33.5"),sQuery(id+"F0.wireOp",EDGE,"E13.33.6"),sQuery(id+"F0.wireOp",EDGE,"E13.33.7"),sQuery(id+"F0.wireOp",EDGE,"E13.33.8"),sQuery(id+"F0.wireOp",EDGE,"E13.33.9"),sQuery(id+"F0.wireOp",EDGE,"E13.33.10"),sQuery(id+"F0.wireOp",EDGE,"E13.33.11"),sQuery(id+"F0.wireOp",EDGE,"E13.34.0"),sQuery(id+"F0.wireOp",EDGE,"E13.34.1"),sQuery(id+"F0.wireOp",EDGE,"E13.34.2"),sQuery(id+"F0.wireOp",EDGE,"E13.34.3"),sQuery(id+"F0.wireOp",EDGE,"E13.34.4"),sQuery(id+"F0.wireOp",EDGE,"E13.34.5"),sQuery(id+"F0.wireOp",EDGE,"E13.34.6"),sQuery(id+"F0.wireOp",EDGE,"E13.34.7"),sQuery(id+"F0.wireOp",EDGE,"E13.34.8"),sQuery(id+"F0.wireOp",EDGE,"E13.34.9"),sQuery(id+"F0.wireOp",EDGE,"E13.34.10"),sQuery(id+"F0.wireOp",EDGE,"E13.34.11"),sQuery(id+"F0.wireOp",EDGE,"E13.35.0"),sQuery(id+"F0.wireOp",EDGE,"E13.35.1"),sQuery(id+"F0.wireOp",EDGE,"E13.35.2"),sQuery(id+"F0.wireOp",EDGE,"E13.35.3"),sQuery(id+"F0.wireOp",EDGE,"E13.35.4"),sQuery(id+"F0.wireOp",EDGE,"E13.35.5"),sQuery(id+"F0.wireOp",EDGE,"E13.35.6"),sQuery(id+"F0.wireOp",EDGE,"E13.35.7"),sQuery(id+"F0.wireOp",EDGE,"E13.35.8"),sQuery(id+"F0.wireOp",EDGE,"E13.35.9"),sQuery(id+"F0.wireOp",EDGE,"E13.35.10"),sQuery(id+"F0.wireOp",EDGE,"E13.35.11"),sQuery(id+"F0.wireOp",EDGE,"E14.trimOffspring"),sQuery(id+"F0.wireOp",EDGE,"E15.trimOffspring"),sQuery(id+"F0.wireOp",EDGE,"E16.trimOffspring"),sQuery(id+"F0.wireOp",EDGE,"E17.trimOffspring"),sQuery(id+"F0.wireOp",EDGE,"E18.trimOffspring"),sQuery(id+"F0.wireOp",EDGE,"E19.trimOffspring"),sQuery(id+"F0.wireOp",EDGE,"E20.trimOffspring"),sQuery(id+"F0.wireOp",EDGE,"E21.trimOffspring"),sQuery(id+"F0.wireOp",EDGE,"E22.trimOffspring"),sQuery(id+"F0.wireOp",EDGE,"E23.trimOffspring"),sQuery(id+"F0.wireOp",EDGE,"E24.trimOffspring"),sQuery(id+"F0.wireOp",EDGE,"E25.trimOffspring"),sQuery(id+"F0.wireOp",EDGE,"E26.trimOffspring"),sQuery(id+"F0.wireOp",EDGE,"E27.trimOffspring"),sQuery(id+"F0.wireOp",EDGE,"E28.trimOffspring"),sQuery(id+"F0.wireOp",EDGE,"E29.trimOffspring"),sQuery(id+"F0.wireOp",EDGE,"E30.trimOffspring"),sQuery(id+"F0.wireOp",EDGE,"E31.trimOffspring"),sQuery(id+"F0.wireOp",EDGE,"E32.trimOffspring"),sQuery(id+"F0.wireOp",EDGE,"E33.trimOffspring"),sQuery(id+"F0.wireOp",EDGE,"E34.trimOffspring"),sQuery(id+"F0.wireOp",EDGE,"E35.trimOffspring"),sQuery(id+"F0.wireOp",EDGE,"E36.trimOffspring"),sQuery(id+"F0.wireOp",EDGE,"E37.trimOffspring"),sQuery(id+"F0.wireOp",EDGE,"E38.trimOffspring"),sQuery(id+"F0.wireOp",EDGE,"E39.trimOffspring"),sQuery(id+"F0.wireOp",EDGE,"E40.trimOffspring"),sQuery(id+"F0.wireOp",EDGE,"E41.trimOffspring"),sQuery(id+"F0.wireOp",EDGE,"E42.trimOffspring"),sQuery(id+"F0.wireOp",EDGE,"E43.trimOffspring"),sQuery(id+"F0.wireOp",EDGE,"E44.trimOffspring"),sQuery(id+"F0.wireOp",EDGE,"E45.trimOffspring"),sQuery(id+"F0.wireOp",EDGE,"E46.trimOffspring"),sQuery(id+"F0.wireOp",EDGE,"E47.trimOffspring"),sQuery(id+"F0.wireOp",EDGE,"E48.trimOffspring")])],"isStart":false});
            var sketch = newSketch(context, id + "F2", { "sketchPlane" : qUnion([Q0])});
            skCircle(sketch, "E49", {"center": v(0, 0) * mm, "radius": 3.18 * mm});
            skSolve(sketch);
        }
        {
            var Q0;
            Q0 = qSketchRegion(id + "F2", true);
            extrude(context, id + "F3", {"entities" : qUnion([Q0]), "operationType" : NewBodyOperationType.REMOVE, "endBound" : BoundingType.THROUGH_ALL, "oppositeDirection" : true, "depth" : 25.4 * mm});
        }
    });
